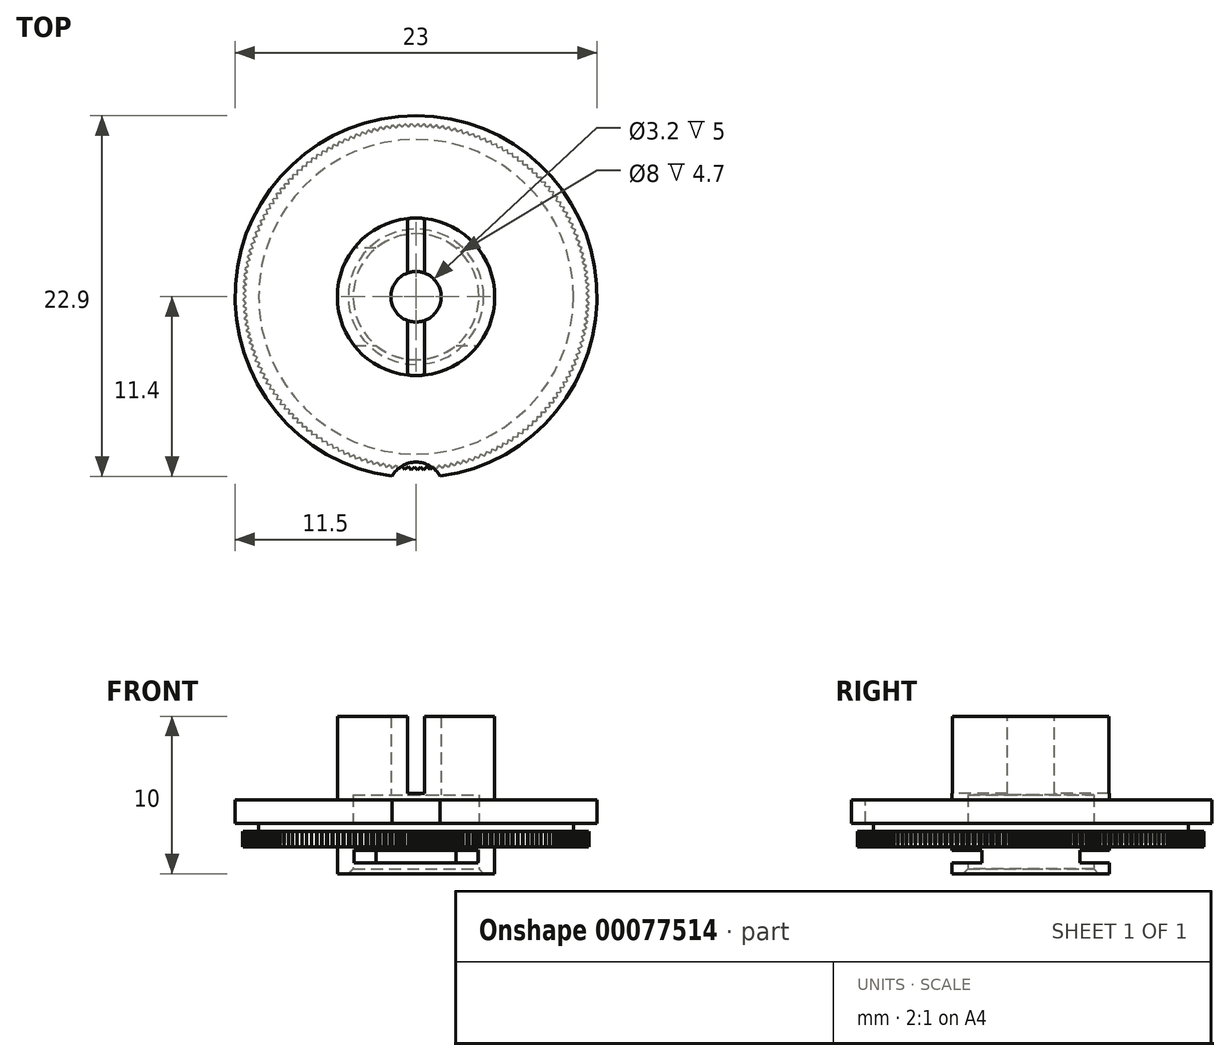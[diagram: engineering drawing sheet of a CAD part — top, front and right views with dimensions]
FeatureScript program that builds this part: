
annotation { "Feature Type Name" : "Feature", "Feature Type Description" : "" }
export const myFeature = defineFeature(function(context is Context, id is Id, definition is map)
    precondition{}
    {
        {
            var Q0;
            Q0=qCreatedBy(makeId("Front.planeOp"),FACE);
            var sketch = newSketch(context, id + "F0", { "sketchPlane" : qUnion([Q0])});
            skLineSegment(sketch, "E0", {"start": v(5, 0) * mm, "end": v(5, 1.7) * mm});
            skLineSegment(sketch, "E1", {"start": v(5, 1.7) * mm, "end": v(11, 1.7) * mm});
            skLineSegment(sketch, "E2", {"start": v(11, 1.7) * mm, "end": v(11, 2.7) * mm});
            skLineSegment(sketch, "E3", {"start": v(11, 2.7) * mm, "end": v(10, 2.7) * mm});
            skLineSegment(sketch, "E4", {"start": v(10, 2.7) * mm, "end": v(10, 3.2) * mm});
            skLineSegment(sketch, "E5", {"start": v(10, 3.2) * mm, "end": v(11.5, 3.2) * mm});
            skLineSegment(sketch, "E6", {"start": v(11.5, 3.2) * mm, "end": v(11.5, 4.7) * mm});
            skLineSegment(sketch, "E7", {"start": v(11.5, 4.7) * mm, "end": v(5, 4.7) * mm});
            skLineSegment(sketch, "E8", {"start": v(5, 4.7) * mm, "end": v(5, 10) * mm});
            skLineSegment(sketch, "E9", {"start": v(5, 10) * mm, "end": v(1.6, 10) * mm});
            skLineSegment(sketch, "E10", {"start": v(1.6, 10) * mm, "end": v(1.6, 5) * mm});
            skLineSegment(sketch, "E11", {"start": v(1.6, 5) * mm, "end": v(4, 5) * mm});
            skLineSegment(sketch, "E12", {"start": v(4, 5) * mm, "end": v(4, 0.3) * mm});
            skLineSegment(sketch, "E13", {"start": v(4, 0.3) * mm, "end": v(4.3, 0) * mm});
            skLineSegment(sketch, "E14", {"start": v(4.3, 0) * mm, "end": v(5, 0) * mm});
            skLineSegment(sketch, "E15", {"start": v(0, 0) * mm, "end": v(0, 10) * mm, "construction": true});
            skSolve(sketch);
        }
        {
            var Q0;
            Q0=makeQuery(id+"F0.imprint","IMPRINT",FACE,{"disambiguationData":[TD([[makeQuery(id+"F0.imprint","IMPRINT",EDGE,{"derivedFrom":sQuery(id+"F0.wireOp",EDGE,"E0")}),1.0]])]});
            var Q1;
            Q1=sQuery(id+"F0.wireOp",EDGE,"E15");
            revolve(context, id + "F1", {"entities" : qUnion([Q0]), "axis" : qUnion([Q1]), "revolveType" : RevolveType.FULL});
        }
        {
            var Q0;
            Q0=makeQuery(id+"F1.opRevolve","SWEPT_FACE",FACE,{"disambiguationData":[OSD([sQuery(id+"F0.wireOp",EDGE,"E1")])]});
            var sketch = newSketch(context, id + "F2", { "sketchPlane" : qUnion([Q0])});
            skCircle(sketch, "E16", {"center": v(0, 0) * mm, "radius": 10.8 * mm});
            skLineSegment(sketch, "E17", {"start": v(-10.8, 0) * mm, "end": v(-11, 0.18) * mm});
            skLineSegment(sketch, "E18", {"start": v(-10.8, 0) * mm, "end": v(-11, -0.22) * mm});
            skLineSegment(sketch, "E19", {"start": v(-10.8, 0) * mm, "end": v(-11, 0) * mm, "construction": true});
            skSolve(sketch);
        }
        {
            var Q0;
            {var subQ2=sQuery(id+"F2.wireOp",EDGE,"E17");Q0=makeQuery(id+"F2.imprint","IMPRINT",FACE,{"disambiguationData":[TD([[makeQuery(id+"F2.imprint","IMPRINT",EDGE,{"derivedFrom":subQ2}),1.0]])]});}
            var Q1;
            Q1=makeQuery(id+"F1.opRevolve","SWEPT_FACE",FACE,{"disambiguationData":[OSD([sQuery(id+"F0.wireOp",EDGE,"E3")])]});
            extrude(context, id + "F3", {"entities" : qUnion([Q0]), "endBound" : BoundingType.UP_TO_SURFACE, "oppositeDirection" : true, "endBoundEntityFace" : qUnion([Q1]), "depth" : 25 * mm});
        }
        {
            var Q0;
            Q0=makeQuery(id+"F3.opExtrude","SWEPT_BODY",BODY,{"disambiguationData":[OSD([sQuery(id+"F0.wireOp",EDGE,"E1"),sQuery(id+"F0.wireOp",EDGE,"E2"),sQuery(id+"F2.wireOp",EDGE,"E17"),sQuery(id+"F2.wireOp",EDGE,"E18")])]});
            var Q1;
            Q1=sQuery(id+"F0.wireOp",EDGE,"E15");
            circularPattern(context, id + "F4", {"entities" : qUnion([Q0]), "axis" : qUnion([Q1]), "angle" : 357.93 * degree, "instanceCount" : round(173), "equalSpace" : true});
        }
        {
            var Q0;
            Q0=makeQuery(id+"F4.opPattern","COPY",BODY,{"derivedFrom":makeQuery(id+"F3.opExtrude","SWEPT_BODY",BODY,{"disambiguationData":[OSD([sQuery(id+"F0.wireOp",EDGE,"E1"),sQuery(id+"F0.wireOp",EDGE,"E2"),sQuery(id+"F2.wireOp",EDGE,"E17"),sQuery(id+"F2.wireOp",EDGE,"E18")])]}),"instanceName":"168"});
            var Q1;
            Q1=makeQuery(id+"F4.opPattern","COPY",BODY,{"derivedFrom":makeQuery(id+"F3.opExtrude","SWEPT_BODY",BODY,{"disambiguationData":[OSD([sQuery(id+"F0.wireOp",EDGE,"E1"),sQuery(id+"F0.wireOp",EDGE,"E2"),sQuery(id+"F2.wireOp",EDGE,"E17"),sQuery(id+"F2.wireOp",EDGE,"E18")])]}),"instanceName":"7"});
            var Q2;
            Q2=makeQuery(id+"F4.opPattern","COPY",BODY,{"derivedFrom":makeQuery(id+"F3.opExtrude","SWEPT_BODY",BODY,{"disambiguationData":[OSD([sQuery(id+"F0.wireOp",EDGE,"E1"),sQuery(id+"F0.wireOp",EDGE,"E2"),sQuery(id+"F2.wireOp",EDGE,"E17"),sQuery(id+"F2.wireOp",EDGE,"E18")])]}),"instanceName":"55"});
            var Q3;
            Q3=makeQuery(id+"F4.opPattern","COPY",BODY,{"derivedFrom":makeQuery(id+"F3.opExtrude","SWEPT_BODY",BODY,{"disambiguationData":[OSD([sQuery(id+"F0.wireOp",EDGE,"E1"),sQuery(id+"F0.wireOp",EDGE,"E2"),sQuery(id+"F2.wireOp",EDGE,"E17"),sQuery(id+"F2.wireOp",EDGE,"E18")])]}),"instanceName":"157"});
            var Q4;
            Q4=makeQuery(id+"F4.opPattern","COPY",BODY,{"derivedFrom":makeQuery(id+"F3.opExtrude","SWEPT_BODY",BODY,{"disambiguationData":[OSD([sQuery(id+"F0.wireOp",EDGE,"E1"),sQuery(id+"F0.wireOp",EDGE,"E2"),sQuery(id+"F2.wireOp",EDGE,"E17"),sQuery(id+"F2.wireOp",EDGE,"E18")])]}),"instanceName":"36"});
            var Q5;
            Q5=makeQuery(id+"F4.opPattern","COPY",BODY,{"derivedFrom":makeQuery(id+"F3.opExtrude","SWEPT_BODY",BODY,{"disambiguationData":[OSD([sQuery(id+"F0.wireOp",EDGE,"E1"),sQuery(id+"F0.wireOp",EDGE,"E2"),sQuery(id+"F2.wireOp",EDGE,"E17"),sQuery(id+"F2.wireOp",EDGE,"E18")])]}),"instanceName":"127"});
            var Q6;
            Q6=makeQuery(id+"F4.opPattern","COPY",BODY,{"derivedFrom":makeQuery(id+"F3.opExtrude","SWEPT_BODY",BODY,{"disambiguationData":[OSD([sQuery(id+"F0.wireOp",EDGE,"E1"),sQuery(id+"F0.wireOp",EDGE,"E2"),sQuery(id+"F2.wireOp",EDGE,"E17"),sQuery(id+"F2.wireOp",EDGE,"E18")])]}),"instanceName":"138"});
            var Q7;
            Q7=makeQuery(id+"F4.opPattern","COPY",BODY,{"derivedFrom":makeQuery(id+"F3.opExtrude","SWEPT_BODY",BODY,{"disambiguationData":[OSD([sQuery(id+"F0.wireOp",EDGE,"E1"),sQuery(id+"F0.wireOp",EDGE,"E2"),sQuery(id+"F2.wireOp",EDGE,"E17"),sQuery(id+"F2.wireOp",EDGE,"E18")])]}),"instanceName":"3"});
            var Q8;
            Q8=makeQuery(id+"F4.opPattern","COPY",BODY,{"derivedFrom":makeQuery(id+"F3.opExtrude","SWEPT_BODY",BODY,{"disambiguationData":[OSD([sQuery(id+"F0.wireOp",EDGE,"E1"),sQuery(id+"F0.wireOp",EDGE,"E2"),sQuery(id+"F2.wireOp",EDGE,"E17"),sQuery(id+"F2.wireOp",EDGE,"E18")])]}),"instanceName":"66"});
            var Q9;
            Q9=makeQuery(id+"F4.opPattern","COPY",BODY,{"derivedFrom":makeQuery(id+"F3.opExtrude","SWEPT_BODY",BODY,{"disambiguationData":[OSD([sQuery(id+"F0.wireOp",EDGE,"E1"),sQuery(id+"F0.wireOp",EDGE,"E2"),sQuery(id+"F2.wireOp",EDGE,"E17"),sQuery(id+"F2.wireOp",EDGE,"E18")])]}),"instanceName":"4"});
            var Q10;
            Q10=makeQuery(id+"F4.opPattern","COPY",BODY,{"derivedFrom":makeQuery(id+"F3.opExtrude","SWEPT_BODY",BODY,{"disambiguationData":[OSD([sQuery(id+"F0.wireOp",EDGE,"E1"),sQuery(id+"F0.wireOp",EDGE,"E2"),sQuery(id+"F2.wireOp",EDGE,"E17"),sQuery(id+"F2.wireOp",EDGE,"E18")])]}),"instanceName":"39"});
            var Q11;
            Q11=makeQuery(id+"F4.opPattern","COPY",BODY,{"derivedFrom":makeQuery(id+"F3.opExtrude","SWEPT_BODY",BODY,{"disambiguationData":[OSD([sQuery(id+"F0.wireOp",EDGE,"E1"),sQuery(id+"F0.wireOp",EDGE,"E2"),sQuery(id+"F2.wireOp",EDGE,"E17"),sQuery(id+"F2.wireOp",EDGE,"E18")])]}),"instanceName":"67"});
            var Q12;
            Q12=makeQuery(id+"F4.opPattern","COPY",BODY,{"derivedFrom":makeQuery(id+"F3.opExtrude","SWEPT_BODY",BODY,{"disambiguationData":[OSD([sQuery(id+"F0.wireOp",EDGE,"E1"),sQuery(id+"F0.wireOp",EDGE,"E2"),sQuery(id+"F2.wireOp",EDGE,"E17"),sQuery(id+"F2.wireOp",EDGE,"E18")])]}),"instanceName":"65"});
            var Q13;
            Q13=makeQuery(id+"F4.opPattern","COPY",BODY,{"derivedFrom":makeQuery(id+"F3.opExtrude","SWEPT_BODY",BODY,{"disambiguationData":[OSD([sQuery(id+"F0.wireOp",EDGE,"E1"),sQuery(id+"F0.wireOp",EDGE,"E2"),sQuery(id+"F2.wireOp",EDGE,"E17"),sQuery(id+"F2.wireOp",EDGE,"E18")])]}),"instanceName":"41"});
            var Q14;
            Q14=makeQuery(id+"F4.opPattern","COPY",BODY,{"derivedFrom":makeQuery(id+"F3.opExtrude","SWEPT_BODY",BODY,{"disambiguationData":[OSD([sQuery(id+"F0.wireOp",EDGE,"E1"),sQuery(id+"F0.wireOp",EDGE,"E2"),sQuery(id+"F2.wireOp",EDGE,"E17"),sQuery(id+"F2.wireOp",EDGE,"E18")])]}),"instanceName":"82"});
            var Q15;
            Q15=makeQuery(id+"F4.opPattern","COPY",BODY,{"derivedFrom":makeQuery(id+"F3.opExtrude","SWEPT_BODY",BODY,{"disambiguationData":[OSD([sQuery(id+"F0.wireOp",EDGE,"E1"),sQuery(id+"F0.wireOp",EDGE,"E2"),sQuery(id+"F2.wireOp",EDGE,"E17"),sQuery(id+"F2.wireOp",EDGE,"E18")])]}),"instanceName":"45"});
            var Q16;
            Q16=makeQuery(id+"F4.opPattern","COPY",BODY,{"derivedFrom":makeQuery(id+"F3.opExtrude","SWEPT_BODY",BODY,{"disambiguationData":[OSD([sQuery(id+"F0.wireOp",EDGE,"E1"),sQuery(id+"F0.wireOp",EDGE,"E2"),sQuery(id+"F2.wireOp",EDGE,"E17"),sQuery(id+"F2.wireOp",EDGE,"E18")])]}),"instanceName":"100"});
            var Q17;
            Q17=makeQuery(id+"F4.opPattern","COPY",BODY,{"derivedFrom":makeQuery(id+"F3.opExtrude","SWEPT_BODY",BODY,{"disambiguationData":[OSD([sQuery(id+"F0.wireOp",EDGE,"E1"),sQuery(id+"F0.wireOp",EDGE,"E2"),sQuery(id+"F2.wireOp",EDGE,"E17"),sQuery(id+"F2.wireOp",EDGE,"E18")])]}),"instanceName":"74"});
            var Q18;
            Q18=makeQuery(id+"F4.opPattern","COPY",BODY,{"derivedFrom":makeQuery(id+"F3.opExtrude","SWEPT_BODY",BODY,{"disambiguationData":[OSD([sQuery(id+"F0.wireOp",EDGE,"E1"),sQuery(id+"F0.wireOp",EDGE,"E2"),sQuery(id+"F2.wireOp",EDGE,"E17"),sQuery(id+"F2.wireOp",EDGE,"E18")])]}),"instanceName":"84"});
            var Q19;
            Q19=makeQuery(id+"F4.opPattern","COPY",BODY,{"derivedFrom":makeQuery(id+"F3.opExtrude","SWEPT_BODY",BODY,{"disambiguationData":[OSD([sQuery(id+"F0.wireOp",EDGE,"E1"),sQuery(id+"F0.wireOp",EDGE,"E2"),sQuery(id+"F2.wireOp",EDGE,"E17"),sQuery(id+"F2.wireOp",EDGE,"E18")])]}),"instanceName":"117"});
            var Q20;
            Q20=makeQuery(id+"F4.opPattern","COPY",BODY,{"derivedFrom":makeQuery(id+"F3.opExtrude","SWEPT_BODY",BODY,{"disambiguationData":[OSD([sQuery(id+"F0.wireOp",EDGE,"E1"),sQuery(id+"F0.wireOp",EDGE,"E2"),sQuery(id+"F2.wireOp",EDGE,"E17"),sQuery(id+"F2.wireOp",EDGE,"E18")])]}),"instanceName":"27"});
            var Q21;
            Q21=makeQuery(id+"F4.opPattern","COPY",BODY,{"derivedFrom":makeQuery(id+"F3.opExtrude","SWEPT_BODY",BODY,{"disambiguationData":[OSD([sQuery(id+"F0.wireOp",EDGE,"E1"),sQuery(id+"F0.wireOp",EDGE,"E2"),sQuery(id+"F2.wireOp",EDGE,"E17"),sQuery(id+"F2.wireOp",EDGE,"E18")])]}),"instanceName":"13"});
            var Q22;
            Q22=makeQuery(id+"F4.opPattern","COPY",BODY,{"derivedFrom":makeQuery(id+"F3.opExtrude","SWEPT_BODY",BODY,{"disambiguationData":[OSD([sQuery(id+"F0.wireOp",EDGE,"E1"),sQuery(id+"F0.wireOp",EDGE,"E2"),sQuery(id+"F2.wireOp",EDGE,"E17"),sQuery(id+"F2.wireOp",EDGE,"E18")])]}),"instanceName":"148"});
            var Q23;
            Q23=makeQuery(id+"F4.opPattern","COPY",BODY,{"derivedFrom":makeQuery(id+"F3.opExtrude","SWEPT_BODY",BODY,{"disambiguationData":[OSD([sQuery(id+"F0.wireOp",EDGE,"E1"),sQuery(id+"F0.wireOp",EDGE,"E2"),sQuery(id+"F2.wireOp",EDGE,"E17"),sQuery(id+"F2.wireOp",EDGE,"E18")])]}),"instanceName":"23"});
            var Q24;
            Q24=makeQuery(id+"F4.opPattern","COPY",BODY,{"derivedFrom":makeQuery(id+"F3.opExtrude","SWEPT_BODY",BODY,{"disambiguationData":[OSD([sQuery(id+"F0.wireOp",EDGE,"E1"),sQuery(id+"F0.wireOp",EDGE,"E2"),sQuery(id+"F2.wireOp",EDGE,"E17"),sQuery(id+"F2.wireOp",EDGE,"E18")])]}),"instanceName":"88"});
            var Q25;
            Q25=makeQuery(id+"F4.opPattern","COPY",BODY,{"derivedFrom":makeQuery(id+"F3.opExtrude","SWEPT_BODY",BODY,{"disambiguationData":[OSD([sQuery(id+"F0.wireOp",EDGE,"E1"),sQuery(id+"F0.wireOp",EDGE,"E2"),sQuery(id+"F2.wireOp",EDGE,"E17"),sQuery(id+"F2.wireOp",EDGE,"E18")])]}),"instanceName":"62"});
            var Q26;
            Q26=makeQuery(id+"F4.opPattern","COPY",BODY,{"derivedFrom":makeQuery(id+"F3.opExtrude","SWEPT_BODY",BODY,{"disambiguationData":[OSD([sQuery(id+"F0.wireOp",EDGE,"E1"),sQuery(id+"F0.wireOp",EDGE,"E2"),sQuery(id+"F2.wireOp",EDGE,"E17"),sQuery(id+"F2.wireOp",EDGE,"E18")])]}),"instanceName":"1"});
            var Q27;
            Q27=makeQuery(id+"F4.opPattern","COPY",BODY,{"derivedFrom":makeQuery(id+"F3.opExtrude","SWEPT_BODY",BODY,{"disambiguationData":[OSD([sQuery(id+"F0.wireOp",EDGE,"E1"),sQuery(id+"F0.wireOp",EDGE,"E2"),sQuery(id+"F2.wireOp",EDGE,"E17"),sQuery(id+"F2.wireOp",EDGE,"E18")])]}),"instanceName":"40"});
            var Q28;
            Q28=makeQuery(id+"F4.opPattern","COPY",BODY,{"derivedFrom":makeQuery(id+"F3.opExtrude","SWEPT_BODY",BODY,{"disambiguationData":[OSD([sQuery(id+"F0.wireOp",EDGE,"E1"),sQuery(id+"F0.wireOp",EDGE,"E2"),sQuery(id+"F2.wireOp",EDGE,"E17"),sQuery(id+"F2.wireOp",EDGE,"E18")])]}),"instanceName":"170"});
            var Q29;
            Q29=makeQuery(id+"F4.opPattern","COPY",BODY,{"derivedFrom":makeQuery(id+"F3.opExtrude","SWEPT_BODY",BODY,{"disambiguationData":[OSD([sQuery(id+"F0.wireOp",EDGE,"E1"),sQuery(id+"F0.wireOp",EDGE,"E2"),sQuery(id+"F2.wireOp",EDGE,"E17"),sQuery(id+"F2.wireOp",EDGE,"E18")])]}),"instanceName":"122"});
            var Q30;
            Q30=makeQuery(id+"F4.opPattern","COPY",BODY,{"derivedFrom":makeQuery(id+"F3.opExtrude","SWEPT_BODY",BODY,{"disambiguationData":[OSD([sQuery(id+"F0.wireOp",EDGE,"E1"),sQuery(id+"F0.wireOp",EDGE,"E2"),sQuery(id+"F2.wireOp",EDGE,"E17"),sQuery(id+"F2.wireOp",EDGE,"E18")])]}),"instanceName":"149"});
            var Q31;
            Q31=makeQuery(id+"F4.opPattern","COPY",BODY,{"derivedFrom":makeQuery(id+"F3.opExtrude","SWEPT_BODY",BODY,{"disambiguationData":[OSD([sQuery(id+"F0.wireOp",EDGE,"E1"),sQuery(id+"F0.wireOp",EDGE,"E2"),sQuery(id+"F2.wireOp",EDGE,"E17"),sQuery(id+"F2.wireOp",EDGE,"E18")])]}),"instanceName":"10"});
            var Q32;
            Q32=makeQuery(id+"F4.opPattern","COPY",BODY,{"derivedFrom":makeQuery(id+"F3.opExtrude","SWEPT_BODY",BODY,{"disambiguationData":[OSD([sQuery(id+"F0.wireOp",EDGE,"E1"),sQuery(id+"F0.wireOp",EDGE,"E2"),sQuery(id+"F2.wireOp",EDGE,"E17"),sQuery(id+"F2.wireOp",EDGE,"E18")])]}),"instanceName":"51"});
            var Q33;
            Q33=makeQuery(id+"F4.opPattern","COPY",BODY,{"derivedFrom":makeQuery(id+"F3.opExtrude","SWEPT_BODY",BODY,{"disambiguationData":[OSD([sQuery(id+"F0.wireOp",EDGE,"E1"),sQuery(id+"F0.wireOp",EDGE,"E2"),sQuery(id+"F2.wireOp",EDGE,"E17"),sQuery(id+"F2.wireOp",EDGE,"E18")])]}),"instanceName":"146"});
            var Q34;
            Q34=makeQuery(id+"F4.opPattern","COPY",BODY,{"derivedFrom":makeQuery(id+"F3.opExtrude","SWEPT_BODY",BODY,{"disambiguationData":[OSD([sQuery(id+"F0.wireOp",EDGE,"E1"),sQuery(id+"F0.wireOp",EDGE,"E2"),sQuery(id+"F2.wireOp",EDGE,"E17"),sQuery(id+"F2.wireOp",EDGE,"E18")])]}),"instanceName":"34"});
            var Q35;
            Q35=makeQuery(id+"F4.opPattern","COPY",BODY,{"derivedFrom":makeQuery(id+"F3.opExtrude","SWEPT_BODY",BODY,{"disambiguationData":[OSD([sQuery(id+"F0.wireOp",EDGE,"E1"),sQuery(id+"F0.wireOp",EDGE,"E2"),sQuery(id+"F2.wireOp",EDGE,"E17"),sQuery(id+"F2.wireOp",EDGE,"E18")])]}),"instanceName":"125"});
            var Q36;
            Q36=makeQuery(id+"F4.opPattern","COPY",BODY,{"derivedFrom":makeQuery(id+"F3.opExtrude","SWEPT_BODY",BODY,{"disambiguationData":[OSD([sQuery(id+"F0.wireOp",EDGE,"E1"),sQuery(id+"F0.wireOp",EDGE,"E2"),sQuery(id+"F2.wireOp",EDGE,"E17"),sQuery(id+"F2.wireOp",EDGE,"E18")])]}),"instanceName":"53"});
            var Q37;
            Q37=makeQuery(id+"F4.opPattern","COPY",BODY,{"derivedFrom":makeQuery(id+"F3.opExtrude","SWEPT_BODY",BODY,{"disambiguationData":[OSD([sQuery(id+"F0.wireOp",EDGE,"E1"),sQuery(id+"F0.wireOp",EDGE,"E2"),sQuery(id+"F2.wireOp",EDGE,"E17"),sQuery(id+"F2.wireOp",EDGE,"E18")])]}),"instanceName":"165"});
            var Q38;
            Q38=makeQuery(id+"F4.opPattern","COPY",BODY,{"derivedFrom":makeQuery(id+"F3.opExtrude","SWEPT_BODY",BODY,{"disambiguationData":[OSD([sQuery(id+"F0.wireOp",EDGE,"E1"),sQuery(id+"F0.wireOp",EDGE,"E2"),sQuery(id+"F2.wireOp",EDGE,"E17"),sQuery(id+"F2.wireOp",EDGE,"E18")])]}),"instanceName":"98"});
            var Q39;
            Q39=makeQuery(id+"F4.opPattern","COPY",BODY,{"derivedFrom":makeQuery(id+"F3.opExtrude","SWEPT_BODY",BODY,{"disambiguationData":[OSD([sQuery(id+"F0.wireOp",EDGE,"E1"),sQuery(id+"F0.wireOp",EDGE,"E2"),sQuery(id+"F2.wireOp",EDGE,"E17"),sQuery(id+"F2.wireOp",EDGE,"E18")])]}),"instanceName":"128"});
            var Q40;
            Q40=makeQuery(id+"F4.opPattern","COPY",BODY,{"derivedFrom":makeQuery(id+"F3.opExtrude","SWEPT_BODY",BODY,{"disambiguationData":[OSD([sQuery(id+"F0.wireOp",EDGE,"E1"),sQuery(id+"F0.wireOp",EDGE,"E2"),sQuery(id+"F2.wireOp",EDGE,"E17"),sQuery(id+"F2.wireOp",EDGE,"E18")])]}),"instanceName":"130"});
            var Q41;
            Q41=makeQuery(id+"F4.opPattern","COPY",BODY,{"derivedFrom":makeQuery(id+"F3.opExtrude","SWEPT_BODY",BODY,{"disambiguationData":[OSD([sQuery(id+"F0.wireOp",EDGE,"E1"),sQuery(id+"F0.wireOp",EDGE,"E2"),sQuery(id+"F2.wireOp",EDGE,"E17"),sQuery(id+"F2.wireOp",EDGE,"E18")])]}),"instanceName":"24"});
            var Q42;
            Q42=makeQuery(id+"F4.opPattern","COPY",BODY,{"derivedFrom":makeQuery(id+"F3.opExtrude","SWEPT_BODY",BODY,{"disambiguationData":[OSD([sQuery(id+"F0.wireOp",EDGE,"E1"),sQuery(id+"F0.wireOp",EDGE,"E2"),sQuery(id+"F2.wireOp",EDGE,"E17"),sQuery(id+"F2.wireOp",EDGE,"E18")])]}),"instanceName":"52"});
            var Q43;
            Q43=makeQuery(id+"F4.opPattern","COPY",BODY,{"derivedFrom":makeQuery(id+"F3.opExtrude","SWEPT_BODY",BODY,{"disambiguationData":[OSD([sQuery(id+"F0.wireOp",EDGE,"E1"),sQuery(id+"F0.wireOp",EDGE,"E2"),sQuery(id+"F2.wireOp",EDGE,"E17"),sQuery(id+"F2.wireOp",EDGE,"E18")])]}),"instanceName":"156"});
            var Q44;
            Q44=makeQuery(id+"F4.opPattern","COPY",BODY,{"derivedFrom":makeQuery(id+"F3.opExtrude","SWEPT_BODY",BODY,{"disambiguationData":[OSD([sQuery(id+"F0.wireOp",EDGE,"E1"),sQuery(id+"F0.wireOp",EDGE,"E2"),sQuery(id+"F2.wireOp",EDGE,"E17"),sQuery(id+"F2.wireOp",EDGE,"E18")])]}),"instanceName":"77"});
            var Q45;
            Q45=makeQuery(id+"F4.opPattern","COPY",BODY,{"derivedFrom":makeQuery(id+"F3.opExtrude","SWEPT_BODY",BODY,{"disambiguationData":[OSD([sQuery(id+"F0.wireOp",EDGE,"E1"),sQuery(id+"F0.wireOp",EDGE,"E2"),sQuery(id+"F2.wireOp",EDGE,"E17"),sQuery(id+"F2.wireOp",EDGE,"E18")])]}),"instanceName":"108"});
            var Q46;
            Q46=makeQuery(id+"F4.opPattern","COPY",BODY,{"derivedFrom":makeQuery(id+"F3.opExtrude","SWEPT_BODY",BODY,{"disambiguationData":[OSD([sQuery(id+"F0.wireOp",EDGE,"E1"),sQuery(id+"F0.wireOp",EDGE,"E2"),sQuery(id+"F2.wireOp",EDGE,"E17"),sQuery(id+"F2.wireOp",EDGE,"E18")])]}),"instanceName":"169"});
            var Q47;
            Q47=makeQuery(id+"F4.opPattern","COPY",BODY,{"derivedFrom":makeQuery(id+"F3.opExtrude","SWEPT_BODY",BODY,{"disambiguationData":[OSD([sQuery(id+"F0.wireOp",EDGE,"E1"),sQuery(id+"F0.wireOp",EDGE,"E2"),sQuery(id+"F2.wireOp",EDGE,"E17"),sQuery(id+"F2.wireOp",EDGE,"E18")])]}),"instanceName":"64"});
            var Q48;
            Q48=makeQuery(id+"F3.opExtrude","SWEPT_BODY",BODY,{"disambiguationData":[OSD([sQuery(id+"F0.wireOp",EDGE,"E1"),sQuery(id+"F0.wireOp",EDGE,"E2"),sQuery(id+"F2.wireOp",EDGE,"E17"),sQuery(id+"F2.wireOp",EDGE,"E18")])]});
            var Q49;
            Q49=makeQuery(id+"F4.opPattern","COPY",BODY,{"derivedFrom":makeQuery(id+"F3.opExtrude","SWEPT_BODY",BODY,{"disambiguationData":[OSD([sQuery(id+"F0.wireOp",EDGE,"E1"),sQuery(id+"F0.wireOp",EDGE,"E2"),sQuery(id+"F2.wireOp",EDGE,"E17"),sQuery(id+"F2.wireOp",EDGE,"E18")])]}),"instanceName":"126"});
            var Q50;
            Q50=makeQuery(id+"F4.opPattern","COPY",BODY,{"derivedFrom":makeQuery(id+"F3.opExtrude","SWEPT_BODY",BODY,{"disambiguationData":[OSD([sQuery(id+"F0.wireOp",EDGE,"E1"),sQuery(id+"F0.wireOp",EDGE,"E2"),sQuery(id+"F2.wireOp",EDGE,"E17"),sQuery(id+"F2.wireOp",EDGE,"E18")])]}),"instanceName":"140"});
            var Q51;
            Q51=makeQuery(id+"F4.opPattern","COPY",BODY,{"derivedFrom":makeQuery(id+"F3.opExtrude","SWEPT_BODY",BODY,{"disambiguationData":[OSD([sQuery(id+"F0.wireOp",EDGE,"E1"),sQuery(id+"F0.wireOp",EDGE,"E2"),sQuery(id+"F2.wireOp",EDGE,"E17"),sQuery(id+"F2.wireOp",EDGE,"E18")])]}),"instanceName":"14"});
            var Q52;
            Q52=makeQuery(id+"F4.opPattern","COPY",BODY,{"derivedFrom":makeQuery(id+"F3.opExtrude","SWEPT_BODY",BODY,{"disambiguationData":[OSD([sQuery(id+"F0.wireOp",EDGE,"E1"),sQuery(id+"F0.wireOp",EDGE,"E2"),sQuery(id+"F2.wireOp",EDGE,"E17"),sQuery(id+"F2.wireOp",EDGE,"E18")])]}),"instanceName":"78"});
            var Q53;
            Q53=makeQuery(id+"F4.opPattern","COPY",BODY,{"derivedFrom":makeQuery(id+"F3.opExtrude","SWEPT_BODY",BODY,{"disambiguationData":[OSD([sQuery(id+"F0.wireOp",EDGE,"E1"),sQuery(id+"F0.wireOp",EDGE,"E2"),sQuery(id+"F2.wireOp",EDGE,"E17"),sQuery(id+"F2.wireOp",EDGE,"E18")])]}),"instanceName":"147"});
            var Q54;
            Q54=makeQuery(id+"F4.opPattern","COPY",BODY,{"derivedFrom":makeQuery(id+"F3.opExtrude","SWEPT_BODY",BODY,{"disambiguationData":[OSD([sQuery(id+"F0.wireOp",EDGE,"E1"),sQuery(id+"F0.wireOp",EDGE,"E2"),sQuery(id+"F2.wireOp",EDGE,"E17"),sQuery(id+"F2.wireOp",EDGE,"E18")])]}),"instanceName":"154"});
            var Q55;
            Q55=makeQuery(id+"F4.opPattern","COPY",BODY,{"derivedFrom":makeQuery(id+"F3.opExtrude","SWEPT_BODY",BODY,{"disambiguationData":[OSD([sQuery(id+"F0.wireOp",EDGE,"E1"),sQuery(id+"F0.wireOp",EDGE,"E2"),sQuery(id+"F2.wireOp",EDGE,"E17"),sQuery(id+"F2.wireOp",EDGE,"E18")])]}),"instanceName":"15"});
            var Q56;
            Q56=makeQuery(id+"F4.opPattern","COPY",BODY,{"derivedFrom":makeQuery(id+"F3.opExtrude","SWEPT_BODY",BODY,{"disambiguationData":[OSD([sQuery(id+"F0.wireOp",EDGE,"E1"),sQuery(id+"F0.wireOp",EDGE,"E2"),sQuery(id+"F2.wireOp",EDGE,"E17"),sQuery(id+"F2.wireOp",EDGE,"E18")])]}),"instanceName":"116"});
            var Q57;
            Q57=makeQuery(id+"F4.opPattern","COPY",BODY,{"derivedFrom":makeQuery(id+"F3.opExtrude","SWEPT_BODY",BODY,{"disambiguationData":[OSD([sQuery(id+"F0.wireOp",EDGE,"E1"),sQuery(id+"F0.wireOp",EDGE,"E2"),sQuery(id+"F2.wireOp",EDGE,"E17"),sQuery(id+"F2.wireOp",EDGE,"E18")])]}),"instanceName":"110"});
            var Q58;
            Q58=makeQuery(id+"F4.opPattern","COPY",BODY,{"derivedFrom":makeQuery(id+"F3.opExtrude","SWEPT_BODY",BODY,{"disambiguationData":[OSD([sQuery(id+"F0.wireOp",EDGE,"E1"),sQuery(id+"F0.wireOp",EDGE,"E2"),sQuery(id+"F2.wireOp",EDGE,"E17"),sQuery(id+"F2.wireOp",EDGE,"E18")])]}),"instanceName":"121"});
            var Q59;
            Q59=makeQuery(id+"F4.opPattern","COPY",BODY,{"derivedFrom":makeQuery(id+"F3.opExtrude","SWEPT_BODY",BODY,{"disambiguationData":[OSD([sQuery(id+"F0.wireOp",EDGE,"E1"),sQuery(id+"F0.wireOp",EDGE,"E2"),sQuery(id+"F2.wireOp",EDGE,"E17"),sQuery(id+"F2.wireOp",EDGE,"E18")])]}),"instanceName":"137"});
            var Q60;
            Q60=makeQuery(id+"F4.opPattern","COPY",BODY,{"derivedFrom":makeQuery(id+"F3.opExtrude","SWEPT_BODY",BODY,{"disambiguationData":[OSD([sQuery(id+"F0.wireOp",EDGE,"E1"),sQuery(id+"F0.wireOp",EDGE,"E2"),sQuery(id+"F2.wireOp",EDGE,"E17"),sQuery(id+"F2.wireOp",EDGE,"E18")])]}),"instanceName":"134"});
            var Q61;
            Q61=makeQuery(id+"F4.opPattern","COPY",BODY,{"derivedFrom":makeQuery(id+"F3.opExtrude","SWEPT_BODY",BODY,{"disambiguationData":[OSD([sQuery(id+"F0.wireOp",EDGE,"E1"),sQuery(id+"F0.wireOp",EDGE,"E2"),sQuery(id+"F2.wireOp",EDGE,"E17"),sQuery(id+"F2.wireOp",EDGE,"E18")])]}),"instanceName":"61"});
            var Q62;
            Q62=makeQuery(id+"F4.opPattern","COPY",BODY,{"derivedFrom":makeQuery(id+"F3.opExtrude","SWEPT_BODY",BODY,{"disambiguationData":[OSD([sQuery(id+"F0.wireOp",EDGE,"E1"),sQuery(id+"F0.wireOp",EDGE,"E2"),sQuery(id+"F2.wireOp",EDGE,"E17"),sQuery(id+"F2.wireOp",EDGE,"E18")])]}),"instanceName":"95"});
            var Q63;
            Q63=makeQuery(id+"F4.opPattern","COPY",BODY,{"derivedFrom":makeQuery(id+"F3.opExtrude","SWEPT_BODY",BODY,{"disambiguationData":[OSD([sQuery(id+"F0.wireOp",EDGE,"E1"),sQuery(id+"F0.wireOp",EDGE,"E2"),sQuery(id+"F2.wireOp",EDGE,"E17"),sQuery(id+"F2.wireOp",EDGE,"E18")])]}),"instanceName":"171"});
            var Q64;
            Q64=makeQuery(id+"F4.opPattern","COPY",BODY,{"derivedFrom":makeQuery(id+"F3.opExtrude","SWEPT_BODY",BODY,{"disambiguationData":[OSD([sQuery(id+"F0.wireOp",EDGE,"E1"),sQuery(id+"F0.wireOp",EDGE,"E2"),sQuery(id+"F2.wireOp",EDGE,"E17"),sQuery(id+"F2.wireOp",EDGE,"E18")])]}),"instanceName":"21"});
            var Q65;
            Q65=makeQuery(id+"F4.opPattern","COPY",BODY,{"derivedFrom":makeQuery(id+"F3.opExtrude","SWEPT_BODY",BODY,{"disambiguationData":[OSD([sQuery(id+"F0.wireOp",EDGE,"E1"),sQuery(id+"F0.wireOp",EDGE,"E2"),sQuery(id+"F2.wireOp",EDGE,"E17"),sQuery(id+"F2.wireOp",EDGE,"E18")])]}),"instanceName":"102"});
            var Q66;
            Q66=makeQuery(id+"F4.opPattern","COPY",BODY,{"derivedFrom":makeQuery(id+"F3.opExtrude","SWEPT_BODY",BODY,{"disambiguationData":[OSD([sQuery(id+"F0.wireOp",EDGE,"E1"),sQuery(id+"F0.wireOp",EDGE,"E2"),sQuery(id+"F2.wireOp",EDGE,"E17"),sQuery(id+"F2.wireOp",EDGE,"E18")])]}),"instanceName":"93"});
            var Q67;
            Q67=makeQuery(id+"F4.opPattern","COPY",BODY,{"derivedFrom":makeQuery(id+"F3.opExtrude","SWEPT_BODY",BODY,{"disambiguationData":[OSD([sQuery(id+"F0.wireOp",EDGE,"E1"),sQuery(id+"F0.wireOp",EDGE,"E2"),sQuery(id+"F2.wireOp",EDGE,"E17"),sQuery(id+"F2.wireOp",EDGE,"E18")])]}),"instanceName":"33"});
            var Q68;
            Q68=makeQuery(id+"F4.opPattern","COPY",BODY,{"derivedFrom":makeQuery(id+"F3.opExtrude","SWEPT_BODY",BODY,{"disambiguationData":[OSD([sQuery(id+"F0.wireOp",EDGE,"E1"),sQuery(id+"F0.wireOp",EDGE,"E2"),sQuery(id+"F2.wireOp",EDGE,"E17"),sQuery(id+"F2.wireOp",EDGE,"E18")])]}),"instanceName":"160"});
            var Q69;
            Q69=makeQuery(id+"F4.opPattern","COPY",BODY,{"derivedFrom":makeQuery(id+"F3.opExtrude","SWEPT_BODY",BODY,{"disambiguationData":[OSD([sQuery(id+"F0.wireOp",EDGE,"E1"),sQuery(id+"F0.wireOp",EDGE,"E2"),sQuery(id+"F2.wireOp",EDGE,"E17"),sQuery(id+"F2.wireOp",EDGE,"E18")])]}),"instanceName":"28"});
            var Q70;
            Q70=makeQuery(id+"F4.opPattern","COPY",BODY,{"derivedFrom":makeQuery(id+"F3.opExtrude","SWEPT_BODY",BODY,{"disambiguationData":[OSD([sQuery(id+"F0.wireOp",EDGE,"E1"),sQuery(id+"F0.wireOp",EDGE,"E2"),sQuery(id+"F2.wireOp",EDGE,"E17"),sQuery(id+"F2.wireOp",EDGE,"E18")])]}),"instanceName":"101"});
            var Q71;
            Q71=makeQuery(id+"F4.opPattern","COPY",BODY,{"derivedFrom":makeQuery(id+"F3.opExtrude","SWEPT_BODY",BODY,{"disambiguationData":[OSD([sQuery(id+"F0.wireOp",EDGE,"E1"),sQuery(id+"F0.wireOp",EDGE,"E2"),sQuery(id+"F2.wireOp",EDGE,"E17"),sQuery(id+"F2.wireOp",EDGE,"E18")])]}),"instanceName":"114"});
            var Q72;
            Q72=makeQuery(id+"F4.opPattern","COPY",BODY,{"derivedFrom":makeQuery(id+"F3.opExtrude","SWEPT_BODY",BODY,{"disambiguationData":[OSD([sQuery(id+"F0.wireOp",EDGE,"E1"),sQuery(id+"F0.wireOp",EDGE,"E2"),sQuery(id+"F2.wireOp",EDGE,"E17"),sQuery(id+"F2.wireOp",EDGE,"E18")])]}),"instanceName":"44"});
            var Q73;
            Q73=makeQuery(id+"F4.opPattern","COPY",BODY,{"derivedFrom":makeQuery(id+"F3.opExtrude","SWEPT_BODY",BODY,{"disambiguationData":[OSD([sQuery(id+"F0.wireOp",EDGE,"E1"),sQuery(id+"F0.wireOp",EDGE,"E2"),sQuery(id+"F2.wireOp",EDGE,"E17"),sQuery(id+"F2.wireOp",EDGE,"E18")])]}),"instanceName":"104"});
            var Q74;
            Q74=makeQuery(id+"F4.opPattern","COPY",BODY,{"derivedFrom":makeQuery(id+"F3.opExtrude","SWEPT_BODY",BODY,{"disambiguationData":[OSD([sQuery(id+"F0.wireOp",EDGE,"E1"),sQuery(id+"F0.wireOp",EDGE,"E2"),sQuery(id+"F2.wireOp",EDGE,"E17"),sQuery(id+"F2.wireOp",EDGE,"E18")])]}),"instanceName":"83"});
            var Q75;
            Q75=makeQuery(id+"F4.opPattern","COPY",BODY,{"derivedFrom":makeQuery(id+"F3.opExtrude","SWEPT_BODY",BODY,{"disambiguationData":[OSD([sQuery(id+"F0.wireOp",EDGE,"E1"),sQuery(id+"F0.wireOp",EDGE,"E2"),sQuery(id+"F2.wireOp",EDGE,"E17"),sQuery(id+"F2.wireOp",EDGE,"E18")])]}),"instanceName":"109"});
            var Q76;
            Q76=makeQuery(id+"F4.opPattern","COPY",BODY,{"derivedFrom":makeQuery(id+"F3.opExtrude","SWEPT_BODY",BODY,{"disambiguationData":[OSD([sQuery(id+"F0.wireOp",EDGE,"E1"),sQuery(id+"F0.wireOp",EDGE,"E2"),sQuery(id+"F2.wireOp",EDGE,"E17"),sQuery(id+"F2.wireOp",EDGE,"E18")])]}),"instanceName":"141"});
            var Q77;
            Q77=makeQuery(id+"F4.opPattern","COPY",BODY,{"derivedFrom":makeQuery(id+"F3.opExtrude","SWEPT_BODY",BODY,{"disambiguationData":[OSD([sQuery(id+"F0.wireOp",EDGE,"E1"),sQuery(id+"F0.wireOp",EDGE,"E2"),sQuery(id+"F2.wireOp",EDGE,"E17"),sQuery(id+"F2.wireOp",EDGE,"E18")])]}),"instanceName":"81"});
            var Q78;
            Q78=makeQuery(id+"F4.opPattern","COPY",BODY,{"derivedFrom":makeQuery(id+"F3.opExtrude","SWEPT_BODY",BODY,{"disambiguationData":[OSD([sQuery(id+"F0.wireOp",EDGE,"E1"),sQuery(id+"F0.wireOp",EDGE,"E2"),sQuery(id+"F2.wireOp",EDGE,"E17"),sQuery(id+"F2.wireOp",EDGE,"E18")])]}),"instanceName":"75"});
            var Q79;
            Q79=makeQuery(id+"F4.opPattern","COPY",BODY,{"derivedFrom":makeQuery(id+"F3.opExtrude","SWEPT_BODY",BODY,{"disambiguationData":[OSD([sQuery(id+"F0.wireOp",EDGE,"E1"),sQuery(id+"F0.wireOp",EDGE,"E2"),sQuery(id+"F2.wireOp",EDGE,"E17"),sQuery(id+"F2.wireOp",EDGE,"E18")])]}),"instanceName":"92"});
            var Q80;
            Q80=makeQuery(id+"F4.opPattern","COPY",BODY,{"derivedFrom":makeQuery(id+"F3.opExtrude","SWEPT_BODY",BODY,{"disambiguationData":[OSD([sQuery(id+"F0.wireOp",EDGE,"E1"),sQuery(id+"F0.wireOp",EDGE,"E2"),sQuery(id+"F2.wireOp",EDGE,"E17"),sQuery(id+"F2.wireOp",EDGE,"E18")])]}),"instanceName":"9"});
            var Q81;
            Q81=makeQuery(id+"F4.opPattern","COPY",BODY,{"derivedFrom":makeQuery(id+"F3.opExtrude","SWEPT_BODY",BODY,{"disambiguationData":[OSD([sQuery(id+"F0.wireOp",EDGE,"E1"),sQuery(id+"F0.wireOp",EDGE,"E2"),sQuery(id+"F2.wireOp",EDGE,"E17"),sQuery(id+"F2.wireOp",EDGE,"E18")])]}),"instanceName":"153"});
            var Q82;
            Q82=makeQuery(id+"F4.opPattern","COPY",BODY,{"derivedFrom":makeQuery(id+"F3.opExtrude","SWEPT_BODY",BODY,{"disambiguationData":[OSD([sQuery(id+"F0.wireOp",EDGE,"E1"),sQuery(id+"F0.wireOp",EDGE,"E2"),sQuery(id+"F2.wireOp",EDGE,"E17"),sQuery(id+"F2.wireOp",EDGE,"E18")])]}),"instanceName":"159"});
            var Q83;
            Q83=makeQuery(id+"F4.opPattern","COPY",BODY,{"derivedFrom":makeQuery(id+"F3.opExtrude","SWEPT_BODY",BODY,{"disambiguationData":[OSD([sQuery(id+"F0.wireOp",EDGE,"E1"),sQuery(id+"F0.wireOp",EDGE,"E2"),sQuery(id+"F2.wireOp",EDGE,"E17"),sQuery(id+"F2.wireOp",EDGE,"E18")])]}),"instanceName":"48"});
            var Q84;
            Q84=makeQuery(id+"F4.opPattern","COPY",BODY,{"derivedFrom":makeQuery(id+"F3.opExtrude","SWEPT_BODY",BODY,{"disambiguationData":[OSD([sQuery(id+"F0.wireOp",EDGE,"E1"),sQuery(id+"F0.wireOp",EDGE,"E2"),sQuery(id+"F2.wireOp",EDGE,"E17"),sQuery(id+"F2.wireOp",EDGE,"E18")])]}),"instanceName":"115"});
            var Q85;
            Q85=makeQuery(id+"F4.opPattern","COPY",BODY,{"derivedFrom":makeQuery(id+"F3.opExtrude","SWEPT_BODY",BODY,{"disambiguationData":[OSD([sQuery(id+"F0.wireOp",EDGE,"E1"),sQuery(id+"F0.wireOp",EDGE,"E2"),sQuery(id+"F2.wireOp",EDGE,"E17"),sQuery(id+"F2.wireOp",EDGE,"E18")])]}),"instanceName":"57"});
            var Q86;
            Q86=makeQuery(id+"F4.opPattern","COPY",BODY,{"derivedFrom":makeQuery(id+"F3.opExtrude","SWEPT_BODY",BODY,{"disambiguationData":[OSD([sQuery(id+"F0.wireOp",EDGE,"E1"),sQuery(id+"F0.wireOp",EDGE,"E2"),sQuery(id+"F2.wireOp",EDGE,"E17"),sQuery(id+"F2.wireOp",EDGE,"E18")])]}),"instanceName":"29"});
            var Q87;
            Q87=makeQuery(id+"F4.opPattern","COPY",BODY,{"derivedFrom":makeQuery(id+"F3.opExtrude","SWEPT_BODY",BODY,{"disambiguationData":[OSD([sQuery(id+"F0.wireOp",EDGE,"E1"),sQuery(id+"F0.wireOp",EDGE,"E2"),sQuery(id+"F2.wireOp",EDGE,"E17"),sQuery(id+"F2.wireOp",EDGE,"E18")])]}),"instanceName":"20"});
            var Q88;
            Q88=makeQuery(id+"F4.opPattern","COPY",BODY,{"derivedFrom":makeQuery(id+"F3.opExtrude","SWEPT_BODY",BODY,{"disambiguationData":[OSD([sQuery(id+"F0.wireOp",EDGE,"E1"),sQuery(id+"F0.wireOp",EDGE,"E2"),sQuery(id+"F2.wireOp",EDGE,"E17"),sQuery(id+"F2.wireOp",EDGE,"E18")])]}),"instanceName":"142"});
            var Q89;
            Q89=makeQuery(id+"F4.opPattern","COPY",BODY,{"derivedFrom":makeQuery(id+"F3.opExtrude","SWEPT_BODY",BODY,{"disambiguationData":[OSD([sQuery(id+"F0.wireOp",EDGE,"E1"),sQuery(id+"F0.wireOp",EDGE,"E2"),sQuery(id+"F2.wireOp",EDGE,"E17"),sQuery(id+"F2.wireOp",EDGE,"E18")])]}),"instanceName":"152"});
            var Q90;
            Q90=makeQuery(id+"F4.opPattern","COPY",BODY,{"derivedFrom":makeQuery(id+"F3.opExtrude","SWEPT_BODY",BODY,{"disambiguationData":[OSD([sQuery(id+"F0.wireOp",EDGE,"E1"),sQuery(id+"F0.wireOp",EDGE,"E2"),sQuery(id+"F2.wireOp",EDGE,"E17"),sQuery(id+"F2.wireOp",EDGE,"E18")])]}),"instanceName":"124"});
            var Q91;
            Q91=makeQuery(id+"F4.opPattern","COPY",BODY,{"derivedFrom":makeQuery(id+"F3.opExtrude","SWEPT_BODY",BODY,{"disambiguationData":[OSD([sQuery(id+"F0.wireOp",EDGE,"E1"),sQuery(id+"F0.wireOp",EDGE,"E2"),sQuery(id+"F2.wireOp",EDGE,"E17"),sQuery(id+"F2.wireOp",EDGE,"E18")])]}),"instanceName":"107"});
            var Q92;
            Q92=makeQuery(id+"F4.opPattern","COPY",BODY,{"derivedFrom":makeQuery(id+"F3.opExtrude","SWEPT_BODY",BODY,{"disambiguationData":[OSD([sQuery(id+"F0.wireOp",EDGE,"E1"),sQuery(id+"F0.wireOp",EDGE,"E2"),sQuery(id+"F2.wireOp",EDGE,"E17"),sQuery(id+"F2.wireOp",EDGE,"E18")])]}),"instanceName":"50"});
            var Q93;
            Q93=makeQuery(id+"F4.opPattern","COPY",BODY,{"derivedFrom":makeQuery(id+"F3.opExtrude","SWEPT_BODY",BODY,{"disambiguationData":[OSD([sQuery(id+"F0.wireOp",EDGE,"E1"),sQuery(id+"F0.wireOp",EDGE,"E2"),sQuery(id+"F2.wireOp",EDGE,"E17"),sQuery(id+"F2.wireOp",EDGE,"E18")])]}),"instanceName":"43"});
            var Q94;
            Q94=makeQuery(id+"F4.opPattern","COPY",BODY,{"derivedFrom":makeQuery(id+"F3.opExtrude","SWEPT_BODY",BODY,{"disambiguationData":[OSD([sQuery(id+"F0.wireOp",EDGE,"E1"),sQuery(id+"F0.wireOp",EDGE,"E2"),sQuery(id+"F2.wireOp",EDGE,"E17"),sQuery(id+"F2.wireOp",EDGE,"E18")])]}),"instanceName":"22"});
            var Q95;
            Q95=makeQuery(id+"F4.opPattern","COPY",BODY,{"derivedFrom":makeQuery(id+"F3.opExtrude","SWEPT_BODY",BODY,{"disambiguationData":[OSD([sQuery(id+"F0.wireOp",EDGE,"E1"),sQuery(id+"F0.wireOp",EDGE,"E2"),sQuery(id+"F2.wireOp",EDGE,"E17"),sQuery(id+"F2.wireOp",EDGE,"E18")])]}),"instanceName":"18"});
            var Q96;
            Q96=makeQuery(id+"F4.opPattern","COPY",BODY,{"derivedFrom":makeQuery(id+"F3.opExtrude","SWEPT_BODY",BODY,{"disambiguationData":[OSD([sQuery(id+"F0.wireOp",EDGE,"E1"),sQuery(id+"F0.wireOp",EDGE,"E2"),sQuery(id+"F2.wireOp",EDGE,"E17"),sQuery(id+"F2.wireOp",EDGE,"E18")])]}),"instanceName":"164"});
            var Q97;
            Q97=makeQuery(id+"F4.opPattern","COPY",BODY,{"derivedFrom":makeQuery(id+"F3.opExtrude","SWEPT_BODY",BODY,{"disambiguationData":[OSD([sQuery(id+"F0.wireOp",EDGE,"E1"),sQuery(id+"F0.wireOp",EDGE,"E2"),sQuery(id+"F2.wireOp",EDGE,"E17"),sQuery(id+"F2.wireOp",EDGE,"E18")])]}),"instanceName":"106"});
            var Q98;
            Q98=makeQuery(id+"F4.opPattern","COPY",BODY,{"derivedFrom":makeQuery(id+"F3.opExtrude","SWEPT_BODY",BODY,{"disambiguationData":[OSD([sQuery(id+"F0.wireOp",EDGE,"E1"),sQuery(id+"F0.wireOp",EDGE,"E2"),sQuery(id+"F2.wireOp",EDGE,"E17"),sQuery(id+"F2.wireOp",EDGE,"E18")])]}),"instanceName":"145"});
            var Q99;
            Q99=makeQuery(id+"F4.opPattern","COPY",BODY,{"derivedFrom":makeQuery(id+"F3.opExtrude","SWEPT_BODY",BODY,{"disambiguationData":[OSD([sQuery(id+"F0.wireOp",EDGE,"E1"),sQuery(id+"F0.wireOp",EDGE,"E2"),sQuery(id+"F2.wireOp",EDGE,"E17"),sQuery(id+"F2.wireOp",EDGE,"E18")])]}),"instanceName":"96"});
            var Q100;
            Q100=makeQuery(id+"F4.opPattern","COPY",BODY,{"derivedFrom":makeQuery(id+"F3.opExtrude","SWEPT_BODY",BODY,{"disambiguationData":[OSD([sQuery(id+"F0.wireOp",EDGE,"E1"),sQuery(id+"F0.wireOp",EDGE,"E2"),sQuery(id+"F2.wireOp",EDGE,"E17"),sQuery(id+"F2.wireOp",EDGE,"E18")])]}),"instanceName":"31"});
            var Q101;
            Q101=makeQuery(id+"F4.opPattern","COPY",BODY,{"derivedFrom":makeQuery(id+"F3.opExtrude","SWEPT_BODY",BODY,{"disambiguationData":[OSD([sQuery(id+"F0.wireOp",EDGE,"E1"),sQuery(id+"F0.wireOp",EDGE,"E2"),sQuery(id+"F2.wireOp",EDGE,"E17"),sQuery(id+"F2.wireOp",EDGE,"E18")])]}),"instanceName":"113"});
            var Q102;
            Q102=makeQuery(id+"F4.opPattern","COPY",BODY,{"derivedFrom":makeQuery(id+"F3.opExtrude","SWEPT_BODY",BODY,{"disambiguationData":[OSD([sQuery(id+"F0.wireOp",EDGE,"E1"),sQuery(id+"F0.wireOp",EDGE,"E2"),sQuery(id+"F2.wireOp",EDGE,"E17"),sQuery(id+"F2.wireOp",EDGE,"E18")])]}),"instanceName":"47"});
            var Q103;
            Q103=makeQuery(id+"F4.opPattern","COPY",BODY,{"derivedFrom":makeQuery(id+"F3.opExtrude","SWEPT_BODY",BODY,{"disambiguationData":[OSD([sQuery(id+"F0.wireOp",EDGE,"E1"),sQuery(id+"F0.wireOp",EDGE,"E2"),sQuery(id+"F2.wireOp",EDGE,"E17"),sQuery(id+"F2.wireOp",EDGE,"E18")])]}),"instanceName":"119"});
            var Q104;
            Q104=makeQuery(id+"F4.opPattern","COPY",BODY,{"derivedFrom":makeQuery(id+"F3.opExtrude","SWEPT_BODY",BODY,{"disambiguationData":[OSD([sQuery(id+"F0.wireOp",EDGE,"E1"),sQuery(id+"F0.wireOp",EDGE,"E2"),sQuery(id+"F2.wireOp",EDGE,"E17"),sQuery(id+"F2.wireOp",EDGE,"E18")])]}),"instanceName":"103"});
            var Q105;
            Q105=makeQuery(id+"F4.opPattern","COPY",BODY,{"derivedFrom":makeQuery(id+"F3.opExtrude","SWEPT_BODY",BODY,{"disambiguationData":[OSD([sQuery(id+"F0.wireOp",EDGE,"E1"),sQuery(id+"F0.wireOp",EDGE,"E2"),sQuery(id+"F2.wireOp",EDGE,"E17"),sQuery(id+"F2.wireOp",EDGE,"E18")])]}),"instanceName":"37"});
            var Q106;
            Q106=makeQuery(id+"F4.opPattern","COPY",BODY,{"derivedFrom":makeQuery(id+"F3.opExtrude","SWEPT_BODY",BODY,{"disambiguationData":[OSD([sQuery(id+"F0.wireOp",EDGE,"E1"),sQuery(id+"F0.wireOp",EDGE,"E2"),sQuery(id+"F2.wireOp",EDGE,"E17"),sQuery(id+"F2.wireOp",EDGE,"E18")])]}),"instanceName":"11"});
            var Q107;
            Q107=makeQuery(id+"F4.opPattern","COPY",BODY,{"derivedFrom":makeQuery(id+"F3.opExtrude","SWEPT_BODY",BODY,{"disambiguationData":[OSD([sQuery(id+"F0.wireOp",EDGE,"E1"),sQuery(id+"F0.wireOp",EDGE,"E2"),sQuery(id+"F2.wireOp",EDGE,"E17"),sQuery(id+"F2.wireOp",EDGE,"E18")])]}),"instanceName":"135"});
            var Q108;
            Q108=makeQuery(id+"F4.opPattern","COPY",BODY,{"derivedFrom":makeQuery(id+"F3.opExtrude","SWEPT_BODY",BODY,{"disambiguationData":[OSD([sQuery(id+"F0.wireOp",EDGE,"E1"),sQuery(id+"F0.wireOp",EDGE,"E2"),sQuery(id+"F2.wireOp",EDGE,"E17"),sQuery(id+"F2.wireOp",EDGE,"E18")])]}),"instanceName":"150"});
            var Q109;
            Q109=makeQuery(id+"F4.opPattern","COPY",BODY,{"derivedFrom":makeQuery(id+"F3.opExtrude","SWEPT_BODY",BODY,{"disambiguationData":[OSD([sQuery(id+"F0.wireOp",EDGE,"E1"),sQuery(id+"F0.wireOp",EDGE,"E2"),sQuery(id+"F2.wireOp",EDGE,"E17"),sQuery(id+"F2.wireOp",EDGE,"E18")])]}),"instanceName":"166"});
            var Q110;
            Q110=makeQuery(id+"F4.opPattern","COPY",BODY,{"derivedFrom":makeQuery(id+"F3.opExtrude","SWEPT_BODY",BODY,{"disambiguationData":[OSD([sQuery(id+"F0.wireOp",EDGE,"E1"),sQuery(id+"F0.wireOp",EDGE,"E2"),sQuery(id+"F2.wireOp",EDGE,"E17"),sQuery(id+"F2.wireOp",EDGE,"E18")])]}),"instanceName":"162"});
            var Q111;
            Q111=makeQuery(id+"F4.opPattern","COPY",BODY,{"derivedFrom":makeQuery(id+"F3.opExtrude","SWEPT_BODY",BODY,{"disambiguationData":[OSD([sQuery(id+"F0.wireOp",EDGE,"E1"),sQuery(id+"F0.wireOp",EDGE,"E2"),sQuery(id+"F2.wireOp",EDGE,"E17"),sQuery(id+"F2.wireOp",EDGE,"E18")])]}),"instanceName":"85"});
            var Q112;
            Q112=makeQuery(id+"F4.opPattern","COPY",BODY,{"derivedFrom":makeQuery(id+"F3.opExtrude","SWEPT_BODY",BODY,{"disambiguationData":[OSD([sQuery(id+"F0.wireOp",EDGE,"E1"),sQuery(id+"F0.wireOp",EDGE,"E2"),sQuery(id+"F2.wireOp",EDGE,"E17"),sQuery(id+"F2.wireOp",EDGE,"E18")])]}),"instanceName":"151"});
            var Q113;
            Q113=makeQuery(id+"F4.opPattern","COPY",BODY,{"derivedFrom":makeQuery(id+"F3.opExtrude","SWEPT_BODY",BODY,{"disambiguationData":[OSD([sQuery(id+"F0.wireOp",EDGE,"E1"),sQuery(id+"F0.wireOp",EDGE,"E2"),sQuery(id+"F2.wireOp",EDGE,"E17"),sQuery(id+"F2.wireOp",EDGE,"E18")])]}),"instanceName":"136"});
            var Q114;
            Q114=makeQuery(id+"F4.opPattern","COPY",BODY,{"derivedFrom":makeQuery(id+"F3.opExtrude","SWEPT_BODY",BODY,{"disambiguationData":[OSD([sQuery(id+"F0.wireOp",EDGE,"E1"),sQuery(id+"F0.wireOp",EDGE,"E2"),sQuery(id+"F2.wireOp",EDGE,"E17"),sQuery(id+"F2.wireOp",EDGE,"E18")])]}),"instanceName":"19"});
            var Q115;
            Q115=makeQuery(id+"F4.opPattern","COPY",BODY,{"derivedFrom":makeQuery(id+"F3.opExtrude","SWEPT_BODY",BODY,{"disambiguationData":[OSD([sQuery(id+"F0.wireOp",EDGE,"E1"),sQuery(id+"F0.wireOp",EDGE,"E2"),sQuery(id+"F2.wireOp",EDGE,"E17"),sQuery(id+"F2.wireOp",EDGE,"E18")])]}),"instanceName":"42"});
            var Q116;
            Q116=makeQuery(id+"F4.opPattern","COPY",BODY,{"derivedFrom":makeQuery(id+"F3.opExtrude","SWEPT_BODY",BODY,{"disambiguationData":[OSD([sQuery(id+"F0.wireOp",EDGE,"E1"),sQuery(id+"F0.wireOp",EDGE,"E2"),sQuery(id+"F2.wireOp",EDGE,"E17"),sQuery(id+"F2.wireOp",EDGE,"E18")])]}),"instanceName":"60"});
            var Q117;
            Q117=makeQuery(id+"F4.opPattern","COPY",BODY,{"derivedFrom":makeQuery(id+"F3.opExtrude","SWEPT_BODY",BODY,{"disambiguationData":[OSD([sQuery(id+"F0.wireOp",EDGE,"E1"),sQuery(id+"F0.wireOp",EDGE,"E2"),sQuery(id+"F2.wireOp",EDGE,"E17"),sQuery(id+"F2.wireOp",EDGE,"E18")])]}),"instanceName":"112"});
            var Q118;
            Q118=makeQuery(id+"F4.opPattern","COPY",BODY,{"derivedFrom":makeQuery(id+"F3.opExtrude","SWEPT_BODY",BODY,{"disambiguationData":[OSD([sQuery(id+"F0.wireOp",EDGE,"E1"),sQuery(id+"F0.wireOp",EDGE,"E2"),sQuery(id+"F2.wireOp",EDGE,"E17"),sQuery(id+"F2.wireOp",EDGE,"E18")])]}),"instanceName":"30"});
            var Q119;
            Q119=makeQuery(id+"F4.opPattern","COPY",BODY,{"derivedFrom":makeQuery(id+"F3.opExtrude","SWEPT_BODY",BODY,{"disambiguationData":[OSD([sQuery(id+"F0.wireOp",EDGE,"E1"),sQuery(id+"F0.wireOp",EDGE,"E2"),sQuery(id+"F2.wireOp",EDGE,"E17"),sQuery(id+"F2.wireOp",EDGE,"E18")])]}),"instanceName":"73"});
            var Q120;
            Q120=makeQuery(id+"F4.opPattern","COPY",BODY,{"derivedFrom":makeQuery(id+"F3.opExtrude","SWEPT_BODY",BODY,{"disambiguationData":[OSD([sQuery(id+"F0.wireOp",EDGE,"E1"),sQuery(id+"F0.wireOp",EDGE,"E2"),sQuery(id+"F2.wireOp",EDGE,"E17"),sQuery(id+"F2.wireOp",EDGE,"E18")])]}),"instanceName":"58"});
            var Q121;
            Q121=makeQuery(id+"F4.opPattern","COPY",BODY,{"derivedFrom":makeQuery(id+"F3.opExtrude","SWEPT_BODY",BODY,{"disambiguationData":[OSD([sQuery(id+"F0.wireOp",EDGE,"E1"),sQuery(id+"F0.wireOp",EDGE,"E2"),sQuery(id+"F2.wireOp",EDGE,"E17"),sQuery(id+"F2.wireOp",EDGE,"E18")])]}),"instanceName":"99"});
            var Q122;
            Q122=makeQuery(id+"F4.opPattern","COPY",BODY,{"derivedFrom":makeQuery(id+"F3.opExtrude","SWEPT_BODY",BODY,{"disambiguationData":[OSD([sQuery(id+"F0.wireOp",EDGE,"E1"),sQuery(id+"F0.wireOp",EDGE,"E2"),sQuery(id+"F2.wireOp",EDGE,"E17"),sQuery(id+"F2.wireOp",EDGE,"E18")])]}),"instanceName":"172"});
            var Q123;
            Q123=makeQuery(id+"F4.opPattern","COPY",BODY,{"derivedFrom":makeQuery(id+"F3.opExtrude","SWEPT_BODY",BODY,{"disambiguationData":[OSD([sQuery(id+"F0.wireOp",EDGE,"E1"),sQuery(id+"F0.wireOp",EDGE,"E2"),sQuery(id+"F2.wireOp",EDGE,"E17"),sQuery(id+"F2.wireOp",EDGE,"E18")])]}),"instanceName":"86"});
            var Q124;
            Q124=makeQuery(id+"F4.opPattern","COPY",BODY,{"derivedFrom":makeQuery(id+"F3.opExtrude","SWEPT_BODY",BODY,{"disambiguationData":[OSD([sQuery(id+"F0.wireOp",EDGE,"E1"),sQuery(id+"F0.wireOp",EDGE,"E2"),sQuery(id+"F2.wireOp",EDGE,"E17"),sQuery(id+"F2.wireOp",EDGE,"E18")])]}),"instanceName":"56"});
            var Q125;
            Q125=makeQuery(id+"F4.opPattern","COPY",BODY,{"derivedFrom":makeQuery(id+"F3.opExtrude","SWEPT_BODY",BODY,{"disambiguationData":[OSD([sQuery(id+"F0.wireOp",EDGE,"E1"),sQuery(id+"F0.wireOp",EDGE,"E2"),sQuery(id+"F2.wireOp",EDGE,"E17"),sQuery(id+"F2.wireOp",EDGE,"E18")])]}),"instanceName":"94"});
            var Q126;
            Q126=makeQuery(id+"F4.opPattern","COPY",BODY,{"derivedFrom":makeQuery(id+"F3.opExtrude","SWEPT_BODY",BODY,{"disambiguationData":[OSD([sQuery(id+"F0.wireOp",EDGE,"E1"),sQuery(id+"F0.wireOp",EDGE,"E2"),sQuery(id+"F2.wireOp",EDGE,"E17"),sQuery(id+"F2.wireOp",EDGE,"E18")])]}),"instanceName":"87"});
            var Q127;
            Q127=makeQuery(id+"F4.opPattern","COPY",BODY,{"derivedFrom":makeQuery(id+"F3.opExtrude","SWEPT_BODY",BODY,{"disambiguationData":[OSD([sQuery(id+"F0.wireOp",EDGE,"E1"),sQuery(id+"F0.wireOp",EDGE,"E2"),sQuery(id+"F2.wireOp",EDGE,"E17"),sQuery(id+"F2.wireOp",EDGE,"E18")])]}),"instanceName":"143"});
            var Q128;
            Q128=makeQuery(id+"F4.opPattern","COPY",BODY,{"derivedFrom":makeQuery(id+"F3.opExtrude","SWEPT_BODY",BODY,{"disambiguationData":[OSD([sQuery(id+"F0.wireOp",EDGE,"E1"),sQuery(id+"F0.wireOp",EDGE,"E2"),sQuery(id+"F2.wireOp",EDGE,"E17"),sQuery(id+"F2.wireOp",EDGE,"E18")])]}),"instanceName":"49"});
            var Q129;
            Q129=makeQuery(id+"F4.opPattern","COPY",BODY,{"derivedFrom":makeQuery(id+"F3.opExtrude","SWEPT_BODY",BODY,{"disambiguationData":[OSD([sQuery(id+"F0.wireOp",EDGE,"E1"),sQuery(id+"F0.wireOp",EDGE,"E2"),sQuery(id+"F2.wireOp",EDGE,"E17"),sQuery(id+"F2.wireOp",EDGE,"E18")])]}),"instanceName":"167"});
            var Q130;
            Q130=makeQuery(id+"F4.opPattern","COPY",BODY,{"derivedFrom":makeQuery(id+"F3.opExtrude","SWEPT_BODY",BODY,{"disambiguationData":[OSD([sQuery(id+"F0.wireOp",EDGE,"E1"),sQuery(id+"F0.wireOp",EDGE,"E2"),sQuery(id+"F2.wireOp",EDGE,"E17"),sQuery(id+"F2.wireOp",EDGE,"E18")])]}),"instanceName":"72"});
            var Q131;
            Q131=makeQuery(id+"F4.opPattern","COPY",BODY,{"derivedFrom":makeQuery(id+"F3.opExtrude","SWEPT_BODY",BODY,{"disambiguationData":[OSD([sQuery(id+"F0.wireOp",EDGE,"E1"),sQuery(id+"F0.wireOp",EDGE,"E2"),sQuery(id+"F2.wireOp",EDGE,"E17"),sQuery(id+"F2.wireOp",EDGE,"E18")])]}),"instanceName":"133"});
            var Q132;
            Q132=makeQuery(id+"F4.opPattern","COPY",BODY,{"derivedFrom":makeQuery(id+"F3.opExtrude","SWEPT_BODY",BODY,{"disambiguationData":[OSD([sQuery(id+"F0.wireOp",EDGE,"E1"),sQuery(id+"F0.wireOp",EDGE,"E2"),sQuery(id+"F2.wireOp",EDGE,"E17"),sQuery(id+"F2.wireOp",EDGE,"E18")])]}),"instanceName":"123"});
            var Q133;
            Q133=makeQuery(id+"F4.opPattern","COPY",BODY,{"derivedFrom":makeQuery(id+"F3.opExtrude","SWEPT_BODY",BODY,{"disambiguationData":[OSD([sQuery(id+"F0.wireOp",EDGE,"E1"),sQuery(id+"F0.wireOp",EDGE,"E2"),sQuery(id+"F2.wireOp",EDGE,"E17"),sQuery(id+"F2.wireOp",EDGE,"E18")])]}),"instanceName":"12"});
            var Q134;
            Q134=makeQuery(id+"F4.opPattern","COPY",BODY,{"derivedFrom":makeQuery(id+"F3.opExtrude","SWEPT_BODY",BODY,{"disambiguationData":[OSD([sQuery(id+"F0.wireOp",EDGE,"E1"),sQuery(id+"F0.wireOp",EDGE,"E2"),sQuery(id+"F2.wireOp",EDGE,"E17"),sQuery(id+"F2.wireOp",EDGE,"E18")])]}),"instanceName":"6"});
            var Q135;
            Q135=makeQuery(id+"F4.opPattern","COPY",BODY,{"derivedFrom":makeQuery(id+"F3.opExtrude","SWEPT_BODY",BODY,{"disambiguationData":[OSD([sQuery(id+"F0.wireOp",EDGE,"E1"),sQuery(id+"F0.wireOp",EDGE,"E2"),sQuery(id+"F2.wireOp",EDGE,"E17"),sQuery(id+"F2.wireOp",EDGE,"E18")])]}),"instanceName":"59"});
            var Q136;
            Q136=makeQuery(id+"F4.opPattern","COPY",BODY,{"derivedFrom":makeQuery(id+"F3.opExtrude","SWEPT_BODY",BODY,{"disambiguationData":[OSD([sQuery(id+"F0.wireOp",EDGE,"E1"),sQuery(id+"F0.wireOp",EDGE,"E2"),sQuery(id+"F2.wireOp",EDGE,"E17"),sQuery(id+"F2.wireOp",EDGE,"E18")])]}),"instanceName":"17"});
            var Q137;
            Q137=makeQuery(id+"F4.opPattern","COPY",BODY,{"derivedFrom":makeQuery(id+"F3.opExtrude","SWEPT_BODY",BODY,{"disambiguationData":[OSD([sQuery(id+"F0.wireOp",EDGE,"E1"),sQuery(id+"F0.wireOp",EDGE,"E2"),sQuery(id+"F2.wireOp",EDGE,"E17"),sQuery(id+"F2.wireOp",EDGE,"E18")])]}),"instanceName":"63"});
            var Q138;
            Q138=makeQuery(id+"F4.opPattern","COPY",BODY,{"derivedFrom":makeQuery(id+"F3.opExtrude","SWEPT_BODY",BODY,{"disambiguationData":[OSD([sQuery(id+"F0.wireOp",EDGE,"E1"),sQuery(id+"F0.wireOp",EDGE,"E2"),sQuery(id+"F2.wireOp",EDGE,"E17"),sQuery(id+"F2.wireOp",EDGE,"E18")])]}),"instanceName":"163"});
            var Q139;
            Q139=makeQuery(id+"F4.opPattern","COPY",BODY,{"derivedFrom":makeQuery(id+"F3.opExtrude","SWEPT_BODY",BODY,{"disambiguationData":[OSD([sQuery(id+"F0.wireOp",EDGE,"E1"),sQuery(id+"F0.wireOp",EDGE,"E2"),sQuery(id+"F2.wireOp",EDGE,"E17"),sQuery(id+"F2.wireOp",EDGE,"E18")])]}),"instanceName":"2"});
            var Q140;
            Q140=makeQuery(id+"F4.opPattern","COPY",BODY,{"derivedFrom":makeQuery(id+"F3.opExtrude","SWEPT_BODY",BODY,{"disambiguationData":[OSD([sQuery(id+"F0.wireOp",EDGE,"E1"),sQuery(id+"F0.wireOp",EDGE,"E2"),sQuery(id+"F2.wireOp",EDGE,"E17"),sQuery(id+"F2.wireOp",EDGE,"E18")])]}),"instanceName":"68"});
            var Q141;
            Q141=makeQuery(id+"F4.opPattern","COPY",BODY,{"derivedFrom":makeQuery(id+"F3.opExtrude","SWEPT_BODY",BODY,{"disambiguationData":[OSD([sQuery(id+"F0.wireOp",EDGE,"E1"),sQuery(id+"F0.wireOp",EDGE,"E2"),sQuery(id+"F2.wireOp",EDGE,"E17"),sQuery(id+"F2.wireOp",EDGE,"E18")])]}),"instanceName":"129"});
            var Q142;
            Q142=makeQuery(id+"F4.opPattern","COPY",BODY,{"derivedFrom":makeQuery(id+"F3.opExtrude","SWEPT_BODY",BODY,{"disambiguationData":[OSD([sQuery(id+"F0.wireOp",EDGE,"E1"),sQuery(id+"F0.wireOp",EDGE,"E2"),sQuery(id+"F2.wireOp",EDGE,"E17"),sQuery(id+"F2.wireOp",EDGE,"E18")])]}),"instanceName":"70"});
            var Q143;
            Q143=makeQuery(id+"F4.opPattern","COPY",BODY,{"derivedFrom":makeQuery(id+"F3.opExtrude","SWEPT_BODY",BODY,{"disambiguationData":[OSD([sQuery(id+"F0.wireOp",EDGE,"E1"),sQuery(id+"F0.wireOp",EDGE,"E2"),sQuery(id+"F2.wireOp",EDGE,"E17"),sQuery(id+"F2.wireOp",EDGE,"E18")])]}),"instanceName":"111"});
            var Q144;
            Q144=makeQuery(id+"F4.opPattern","COPY",BODY,{"derivedFrom":makeQuery(id+"F3.opExtrude","SWEPT_BODY",BODY,{"disambiguationData":[OSD([sQuery(id+"F0.wireOp",EDGE,"E1"),sQuery(id+"F0.wireOp",EDGE,"E2"),sQuery(id+"F2.wireOp",EDGE,"E17"),sQuery(id+"F2.wireOp",EDGE,"E18")])]}),"instanceName":"16"});
            var Q145;
            Q145=makeQuery(id+"F4.opPattern","COPY",BODY,{"derivedFrom":makeQuery(id+"F3.opExtrude","SWEPT_BODY",BODY,{"disambiguationData":[OSD([sQuery(id+"F0.wireOp",EDGE,"E1"),sQuery(id+"F0.wireOp",EDGE,"E2"),sQuery(id+"F2.wireOp",EDGE,"E17"),sQuery(id+"F2.wireOp",EDGE,"E18")])]}),"instanceName":"144"});
            var Q146;
            Q146=makeQuery(id+"F4.opPattern","COPY",BODY,{"derivedFrom":makeQuery(id+"F3.opExtrude","SWEPT_BODY",BODY,{"disambiguationData":[OSD([sQuery(id+"F0.wireOp",EDGE,"E1"),sQuery(id+"F0.wireOp",EDGE,"E2"),sQuery(id+"F2.wireOp",EDGE,"E17"),sQuery(id+"F2.wireOp",EDGE,"E18")])]}),"instanceName":"139"});
            var Q147;
            Q147=makeQuery(id+"F4.opPattern","COPY",BODY,{"derivedFrom":makeQuery(id+"F3.opExtrude","SWEPT_BODY",BODY,{"disambiguationData":[OSD([sQuery(id+"F0.wireOp",EDGE,"E1"),sQuery(id+"F0.wireOp",EDGE,"E2"),sQuery(id+"F2.wireOp",EDGE,"E17"),sQuery(id+"F2.wireOp",EDGE,"E18")])]}),"instanceName":"38"});
            var Q148;
            Q148=makeQuery(id+"F4.opPattern","COPY",BODY,{"derivedFrom":makeQuery(id+"F3.opExtrude","SWEPT_BODY",BODY,{"disambiguationData":[OSD([sQuery(id+"F0.wireOp",EDGE,"E1"),sQuery(id+"F0.wireOp",EDGE,"E2"),sQuery(id+"F2.wireOp",EDGE,"E17"),sQuery(id+"F2.wireOp",EDGE,"E18")])]}),"instanceName":"120"});
            var Q149;
            Q149=makeQuery(id+"F4.opPattern","COPY",BODY,{"derivedFrom":makeQuery(id+"F3.opExtrude","SWEPT_BODY",BODY,{"disambiguationData":[OSD([sQuery(id+"F0.wireOp",EDGE,"E1"),sQuery(id+"F0.wireOp",EDGE,"E2"),sQuery(id+"F2.wireOp",EDGE,"E17"),sQuery(id+"F2.wireOp",EDGE,"E18")])]}),"instanceName":"32"});
            var Q150;
            Q150=makeQuery(id+"F4.opPattern","COPY",BODY,{"derivedFrom":makeQuery(id+"F3.opExtrude","SWEPT_BODY",BODY,{"disambiguationData":[OSD([sQuery(id+"F0.wireOp",EDGE,"E1"),sQuery(id+"F0.wireOp",EDGE,"E2"),sQuery(id+"F2.wireOp",EDGE,"E17"),sQuery(id+"F2.wireOp",EDGE,"E18")])]}),"instanceName":"105"});
            var Q151;
            Q151=makeQuery(id+"F4.opPattern","COPY",BODY,{"derivedFrom":makeQuery(id+"F3.opExtrude","SWEPT_BODY",BODY,{"disambiguationData":[OSD([sQuery(id+"F0.wireOp",EDGE,"E1"),sQuery(id+"F0.wireOp",EDGE,"E2"),sQuery(id+"F2.wireOp",EDGE,"E17"),sQuery(id+"F2.wireOp",EDGE,"E18")])]}),"instanceName":"35"});
            var Q152;
            Q152=makeQuery(id+"F4.opPattern","COPY",BODY,{"derivedFrom":makeQuery(id+"F3.opExtrude","SWEPT_BODY",BODY,{"disambiguationData":[OSD([sQuery(id+"F0.wireOp",EDGE,"E1"),sQuery(id+"F0.wireOp",EDGE,"E2"),sQuery(id+"F2.wireOp",EDGE,"E17"),sQuery(id+"F2.wireOp",EDGE,"E18")])]}),"instanceName":"132"});
            var Q153;
            Q153=makeQuery(id+"F4.opPattern","COPY",BODY,{"derivedFrom":makeQuery(id+"F3.opExtrude","SWEPT_BODY",BODY,{"disambiguationData":[OSD([sQuery(id+"F0.wireOp",EDGE,"E1"),sQuery(id+"F0.wireOp",EDGE,"E2"),sQuery(id+"F2.wireOp",EDGE,"E17"),sQuery(id+"F2.wireOp",EDGE,"E18")])]}),"instanceName":"69"});
            var Q154;
            Q154=makeQuery(id+"F4.opPattern","COPY",BODY,{"derivedFrom":makeQuery(id+"F3.opExtrude","SWEPT_BODY",BODY,{"disambiguationData":[OSD([sQuery(id+"F0.wireOp",EDGE,"E1"),sQuery(id+"F0.wireOp",EDGE,"E2"),sQuery(id+"F2.wireOp",EDGE,"E17"),sQuery(id+"F2.wireOp",EDGE,"E18")])]}),"instanceName":"79"});
            var Q155;
            Q155=makeQuery(id+"F4.opPattern","COPY",BODY,{"derivedFrom":makeQuery(id+"F3.opExtrude","SWEPT_BODY",BODY,{"disambiguationData":[OSD([sQuery(id+"F0.wireOp",EDGE,"E1"),sQuery(id+"F0.wireOp",EDGE,"E2"),sQuery(id+"F2.wireOp",EDGE,"E17"),sQuery(id+"F2.wireOp",EDGE,"E18")])]}),"instanceName":"131"});
            var Q156;
            Q156=makeQuery(id+"F4.opPattern","COPY",BODY,{"derivedFrom":makeQuery(id+"F3.opExtrude","SWEPT_BODY",BODY,{"disambiguationData":[OSD([sQuery(id+"F0.wireOp",EDGE,"E1"),sQuery(id+"F0.wireOp",EDGE,"E2"),sQuery(id+"F2.wireOp",EDGE,"E17"),sQuery(id+"F2.wireOp",EDGE,"E18")])]}),"instanceName":"26"});
            var Q157;
            Q157=makeQuery(id+"F4.opPattern","COPY",BODY,{"derivedFrom":makeQuery(id+"F3.opExtrude","SWEPT_BODY",BODY,{"disambiguationData":[OSD([sQuery(id+"F0.wireOp",EDGE,"E1"),sQuery(id+"F0.wireOp",EDGE,"E2"),sQuery(id+"F2.wireOp",EDGE,"E17"),sQuery(id+"F2.wireOp",EDGE,"E18")])]}),"instanceName":"158"});
            var Q158;
            Q158=makeQuery(id+"F4.opPattern","COPY",BODY,{"derivedFrom":makeQuery(id+"F3.opExtrude","SWEPT_BODY",BODY,{"disambiguationData":[OSD([sQuery(id+"F0.wireOp",EDGE,"E1"),sQuery(id+"F0.wireOp",EDGE,"E2"),sQuery(id+"F2.wireOp",EDGE,"E17"),sQuery(id+"F2.wireOp",EDGE,"E18")])]}),"instanceName":"91"});
            var Q159;
            Q159=makeQuery(id+"F4.opPattern","COPY",BODY,{"derivedFrom":makeQuery(id+"F3.opExtrude","SWEPT_BODY",BODY,{"disambiguationData":[OSD([sQuery(id+"F0.wireOp",EDGE,"E1"),sQuery(id+"F0.wireOp",EDGE,"E2"),sQuery(id+"F2.wireOp",EDGE,"E17"),sQuery(id+"F2.wireOp",EDGE,"E18")])]}),"instanceName":"118"});
            var Q160;
            Q160=makeQuery(id+"F4.opPattern","COPY",BODY,{"derivedFrom":makeQuery(id+"F3.opExtrude","SWEPT_BODY",BODY,{"disambiguationData":[OSD([sQuery(id+"F0.wireOp",EDGE,"E1"),sQuery(id+"F0.wireOp",EDGE,"E2"),sQuery(id+"F2.wireOp",EDGE,"E17"),sQuery(id+"F2.wireOp",EDGE,"E18")])]}),"instanceName":"90"});
            var Q161;
            Q161=makeQuery(id+"F4.opPattern","COPY",BODY,{"derivedFrom":makeQuery(id+"F3.opExtrude","SWEPT_BODY",BODY,{"disambiguationData":[OSD([sQuery(id+"F0.wireOp",EDGE,"E1"),sQuery(id+"F0.wireOp",EDGE,"E2"),sQuery(id+"F2.wireOp",EDGE,"E17"),sQuery(id+"F2.wireOp",EDGE,"E18")])]}),"instanceName":"8"});
            var Q162;
            Q162=makeQuery(id+"F4.opPattern","COPY",BODY,{"derivedFrom":makeQuery(id+"F3.opExtrude","SWEPT_BODY",BODY,{"disambiguationData":[OSD([sQuery(id+"F0.wireOp",EDGE,"E1"),sQuery(id+"F0.wireOp",EDGE,"E2"),sQuery(id+"F2.wireOp",EDGE,"E17"),sQuery(id+"F2.wireOp",EDGE,"E18")])]}),"instanceName":"76"});
            var Q163;
            Q163=makeQuery(id+"F4.opPattern","COPY",BODY,{"derivedFrom":makeQuery(id+"F3.opExtrude","SWEPT_BODY",BODY,{"disambiguationData":[OSD([sQuery(id+"F0.wireOp",EDGE,"E1"),sQuery(id+"F0.wireOp",EDGE,"E2"),sQuery(id+"F2.wireOp",EDGE,"E17"),sQuery(id+"F2.wireOp",EDGE,"E18")])]}),"instanceName":"54"});
            var Q164;
            Q164=makeQuery(id+"F4.opPattern","COPY",BODY,{"derivedFrom":makeQuery(id+"F3.opExtrude","SWEPT_BODY",BODY,{"disambiguationData":[OSD([sQuery(id+"F0.wireOp",EDGE,"E1"),sQuery(id+"F0.wireOp",EDGE,"E2"),sQuery(id+"F2.wireOp",EDGE,"E17"),sQuery(id+"F2.wireOp",EDGE,"E18")])]}),"instanceName":"97"});
            var Q165;
            Q165=makeQuery(id+"F4.opPattern","COPY",BODY,{"derivedFrom":makeQuery(id+"F3.opExtrude","SWEPT_BODY",BODY,{"disambiguationData":[OSD([sQuery(id+"F0.wireOp",EDGE,"E1"),sQuery(id+"F0.wireOp",EDGE,"E2"),sQuery(id+"F2.wireOp",EDGE,"E17"),sQuery(id+"F2.wireOp",EDGE,"E18")])]}),"instanceName":"5"});
            var Q166;
            Q166=makeQuery(id+"F4.opPattern","COPY",BODY,{"derivedFrom":makeQuery(id+"F3.opExtrude","SWEPT_BODY",BODY,{"disambiguationData":[OSD([sQuery(id+"F0.wireOp",EDGE,"E1"),sQuery(id+"F0.wireOp",EDGE,"E2"),sQuery(id+"F2.wireOp",EDGE,"E17"),sQuery(id+"F2.wireOp",EDGE,"E18")])]}),"instanceName":"161"});
            var Q167;
            Q167=makeQuery(id+"F4.opPattern","COPY",BODY,{"derivedFrom":makeQuery(id+"F3.opExtrude","SWEPT_BODY",BODY,{"disambiguationData":[OSD([sQuery(id+"F0.wireOp",EDGE,"E1"),sQuery(id+"F0.wireOp",EDGE,"E2"),sQuery(id+"F2.wireOp",EDGE,"E17"),sQuery(id+"F2.wireOp",EDGE,"E18")])]}),"instanceName":"46"});
            var Q168;
            Q168=makeQuery(id+"F4.opPattern","COPY",BODY,{"derivedFrom":makeQuery(id+"F3.opExtrude","SWEPT_BODY",BODY,{"disambiguationData":[OSD([sQuery(id+"F0.wireOp",EDGE,"E1"),sQuery(id+"F0.wireOp",EDGE,"E2"),sQuery(id+"F2.wireOp",EDGE,"E17"),sQuery(id+"F2.wireOp",EDGE,"E18")])]}),"instanceName":"71"});
            var Q169;
            Q169=makeQuery(id+"F4.opPattern","COPY",BODY,{"derivedFrom":makeQuery(id+"F3.opExtrude","SWEPT_BODY",BODY,{"disambiguationData":[OSD([sQuery(id+"F0.wireOp",EDGE,"E1"),sQuery(id+"F0.wireOp",EDGE,"E2"),sQuery(id+"F2.wireOp",EDGE,"E17"),sQuery(id+"F2.wireOp",EDGE,"E18")])]}),"instanceName":"80"});
            var Q170;
            Q170=makeQuery(id+"F4.opPattern","COPY",BODY,{"derivedFrom":makeQuery(id+"F3.opExtrude","SWEPT_BODY",BODY,{"disambiguationData":[OSD([sQuery(id+"F0.wireOp",EDGE,"E1"),sQuery(id+"F0.wireOp",EDGE,"E2"),sQuery(id+"F2.wireOp",EDGE,"E17"),sQuery(id+"F2.wireOp",EDGE,"E18")])]}),"instanceName":"25"});
            var Q171;
            Q171=makeQuery(id+"F4.opPattern","COPY",BODY,{"derivedFrom":makeQuery(id+"F3.opExtrude","SWEPT_BODY",BODY,{"disambiguationData":[OSD([sQuery(id+"F0.wireOp",EDGE,"E1"),sQuery(id+"F0.wireOp",EDGE,"E2"),sQuery(id+"F2.wireOp",EDGE,"E17"),sQuery(id+"F2.wireOp",EDGE,"E18")])]}),"instanceName":"155"});
            var Q172;
            Q172=makeQuery(id+"F4.opPattern","COPY",BODY,{"derivedFrom":makeQuery(id+"F3.opExtrude","SWEPT_BODY",BODY,{"disambiguationData":[OSD([sQuery(id+"F0.wireOp",EDGE,"E1"),sQuery(id+"F0.wireOp",EDGE,"E2"),sQuery(id+"F2.wireOp",EDGE,"E17"),sQuery(id+"F2.wireOp",EDGE,"E18")])]}),"instanceName":"89"});
            var Q173;
            Q173=makeQuery(id+"F1.opRevolve","SWEPT_BODY",BODY,{"disambiguationData":[OSD([sQuery(id+"F0.wireOp",EDGE,"E0"),sQuery(id+"F0.wireOp",EDGE,"E1"),sQuery(id+"F0.wireOp",EDGE,"E2"),sQuery(id+"F0.wireOp",EDGE,"E3"),sQuery(id+"F0.wireOp",EDGE,"E4"),sQuery(id+"F0.wireOp",EDGE,"E5"),sQuery(id+"F0.wireOp",EDGE,"E6"),sQuery(id+"F0.wireOp",EDGE,"E7"),sQuery(id+"F0.wireOp",EDGE,"E8"),sQuery(id+"F0.wireOp",EDGE,"E9"),sQuery(id+"F0.wireOp",EDGE,"E10"),sQuery(id+"F0.wireOp",EDGE,"E11"),sQuery(id+"F0.wireOp",EDGE,"E12"),sQuery(id+"F0.wireOp",EDGE,"E13"),sQuery(id+"F0.wireOp",EDGE,"E14")])]});
            booleanBodies(context, id + "F5", {"operationType" : BooleanOperationType.SUBTRACTION, "tools" : qUnion([Q0, Q1, Q2, Q3, Q4, Q5, Q6, Q7, Q8, Q9, Q10, Q11, Q12, Q13, Q14, Q15, Q16, Q17, Q18, Q19, Q20, Q21, Q22, Q23, Q24, Q25, Q26, Q27, Q28, Q29, Q30, Q31, Q32, Q33, Q34, Q35, Q36, Q37, Q38, Q39, Q40, Q41, Q42, Q43, Q44, Q45, Q46, Q47, Q48, Q49, Q50, Q51, Q52, Q53, Q54, Q55, Q56, Q57, Q58, Q59, Q60, Q61, Q62, Q63, Q64, Q65, Q66, Q67, Q68, Q69, Q70, Q71, Q72, Q73, Q74, Q75, Q76, Q77, Q78, Q79, Q80, Q81, Q82, Q83, Q84, Q85, Q86, Q87, Q88, Q89, Q90, Q91, Q92, Q93, Q94, Q95, Q96, Q97, Q98, Q99, Q100, Q101, Q102, Q103, Q104, Q105, Q106, Q107, Q108, Q109, Q110, Q111, Q112, Q113, Q114, Q115, Q116, Q117, Q118, Q119, Q120, Q121, Q122, Q123, Q124, Q125, Q126, Q127, Q128, Q129, Q130, Q131, Q132, Q133, Q134, Q135, Q136, Q137, Q138, Q139, Q140, Q141, Q142, Q143, Q144, Q145, Q146, Q147, Q148, Q149, Q150, Q151, Q152, Q153, Q154, Q155, Q156, Q157, Q158, Q159, Q160, Q161, Q162, Q163, Q164, Q165, Q166, Q167, Q168, Q169, Q170, Q171, Q172]), "targets" : qUnion([Q173])});
        }
        {
            var Q0;
            Q0=makeQuery(id+"F1.opRevolve","SWEPT_FACE",FACE,{"disambiguationData":[OSD([sQuery(id+"F0.wireOp",EDGE,"E7")])]});
            cPlane(context, id + "F6", {"entities" : qUnion([Q0]), "cplaneType" : CPlaneType.OFFSET, "offset" : 3.2 * mm, "oppositeDirection" : true, "width" : 150 * mm, "height" : 150 * mm});
        }
        {
            var Q0;
            Q0=qCreatedBy(id+"F6.planeOp",FACE);
            var sketch = newSketch(context, id + "F7", { "sketchPlane" : qUnion([Q0])});
            skCircle(sketch, "E20", {"center": v(0, 0) * mm, "radius": 5 * mm});
            skLineSegment(sketch, "E21", {"start": v(-3.92, -3.1) * mm, "end": v(3.92, -3.1) * mm});
            skLineSegment(sketch, "E22", {"start": v(3.92, 3.1) * mm, "end": v(-3.92, 3.1) * mm});
            skSolve(sketch);
        }
        {
            var Q0;
            {var subQ0=sQuery(id+"F7.wireOp",EDGE,"E21");Q0=makeQuery(id+"F7.imprint","IMPRINT",FACE,{"disambiguationData":[TD([[makeQuery(id+"F7.imprint","IMPRINT",EDGE,{"derivedFrom":subQ0}),-1.0]])]});}
            var Q1;
            {var subQ0=sQuery(id+"F7.wireOp",EDGE,"E22");Q1=makeQuery(id+"F7.imprint","IMPRINT",FACE,{"disambiguationData":[TD([[makeQuery(id+"F7.imprint","IMPRINT",EDGE,{"derivedFrom":subQ0}),-1.0]])]});}
            extrude(context, id + "F8", {"entities" : qUnion([Q0, Q1]), "operationType" : NewBodyOperationType.REMOVE, "oppositeDirection" : true, "depth" : 0.8 * mm});
        }
        {
            var Q0;
            Q0=makeQuery(id+"F1.opRevolve","SWEPT_FACE",FACE,{"disambiguationData":[OSD([sQuery(id+"F0.wireOp",EDGE,"E7")])]});
            var sketch = newSketch(context, id + "F9", { "sketchPlane" : qUnion([Q0])});
            skCircle(sketch, "E23", {"center": v(0, -12.25) * mm, "radius": 1.75 * mm});
            skLineSegment(sketch, "E24", {"start": v(-0.45, -10.56) * mm, "end": v(-6.76, -12.25) * mm});
            skLineSegment(sketch, "E25", {"start": v(-6.76, -12.25) * mm, "end": v(0, -12.25) * mm, "construction": true});
            skSolve(sketch);
        }
        {
            var Q0;
            {var subQ1=sQuery(id+"F9.wireOp",EDGE,"E23");var subQ4=makeQuery(id+"F9.imprint","INTERSECT",VERTEX,{"derivedFrom":[subQ1,sQuery(id+"F9.wireOp",EDGE,"E24")]});Q0=makeQuery(id+"F9.imprint","IMPRINT",FACE,{"disambiguationData":[TD([[makeQuery(id+"F9.imprint","IMPRINT",EDGE,{"disambiguationData":[TD([[subQ4,1.0]])],"derivedFrom":subQ1}),1.0]])]});}
            var Q1;
            Q1=makeQuery(id+"F1.opRevolve","SWEPT_FACE",FACE,{"disambiguationData":[OSD([sQuery(id+"F0.wireOp",EDGE,"E5")])]});
            extrude(context, id + "F10", {"entities" : qUnion([Q0]), "operationType" : NewBodyOperationType.REMOVE, "endBound" : BoundingType.UP_TO_SURFACE, "oppositeDirection" : true, "endBoundEntityFace" : qUnion([Q1]), "depth" : 25 * mm});
        }
        {
            var Q0;
            Q0=makeQuery(id+"F1.opRevolve","SWEPT_FACE",FACE,{"disambiguationData":[OSD([sQuery(id+"F0.wireOp",EDGE,"E9")])]});
            var sketch = newSketch(context, id + "F11", { "sketchPlane" : qUnion([Q0])});
            skLineSegment(sketch, "E26", {"start": v(-0.55, 4.97) * mm, "end": v(-0.55, -4.97) * mm});
            skLineSegment(sketch, "E27", {"start": v(0.55, -4.97) * mm, "end": v(0.55, 4.97) * mm});
            skSolve(sketch);
        }
        {
            var Q0;
            {var subQ0=sQuery(id+"F0.wireOp",EDGE,"E9");var subQ4=sQuery(id+"F11.wireOp",EDGE,"E26");var subQ6=makeQuery(id+"F1.opRevolve","SWEPT_EDGE",EDGE,{"disambiguationData":[OSD([sQuery(id+"F0.wireOp",EDGE,"E8"),subQ0])]});var subQ8=makeQuery(id+"F11.imprint","INTERSECT",VERTEX,{"disambiguationData":[OD(0.0)],"derivedFrom":[subQ6,subQ4]});Q0=makeQuery(id+"F11.imprint","IMPRINT",FACE,{"disambiguationData":[TD([[makeQuery(id+"F11.imprint","IMPRINT",EDGE,{"disambiguationData":[TD([[subQ8,-1.0]])],"derivedFrom":subQ4}),1.0]])]});}
            var Q1;
            {var subQ0=sQuery(id+"F0.wireOp",EDGE,"E9");var subQ4=sQuery(id+"F11.wireOp",EDGE,"E26");var subQ6=makeQuery(id+"F1.opRevolve","SWEPT_EDGE",EDGE,{"disambiguationData":[OSD([sQuery(id+"F0.wireOp",EDGE,"E8"),subQ0])]});var subQ8=makeQuery(id+"F11.imprint","INTERSECT",VERTEX,{"disambiguationData":[OD(1.0)],"derivedFrom":[subQ6,subQ4]});Q1=makeQuery(id+"F11.imprint","IMPRINT",FACE,{"disambiguationData":[TD([[makeQuery(id+"F11.imprint","IMPRINT",EDGE,{"disambiguationData":[TD([[subQ8,1.0]])],"derivedFrom":subQ4}),1.0]])]});}
            extrude(context, id + "F12", {"entities" : qUnion([Q0, Q1]), "operationType" : NewBodyOperationType.REMOVE, "oppositeDirection" : true, "depth" : 4.9 * mm});
        }
    });
